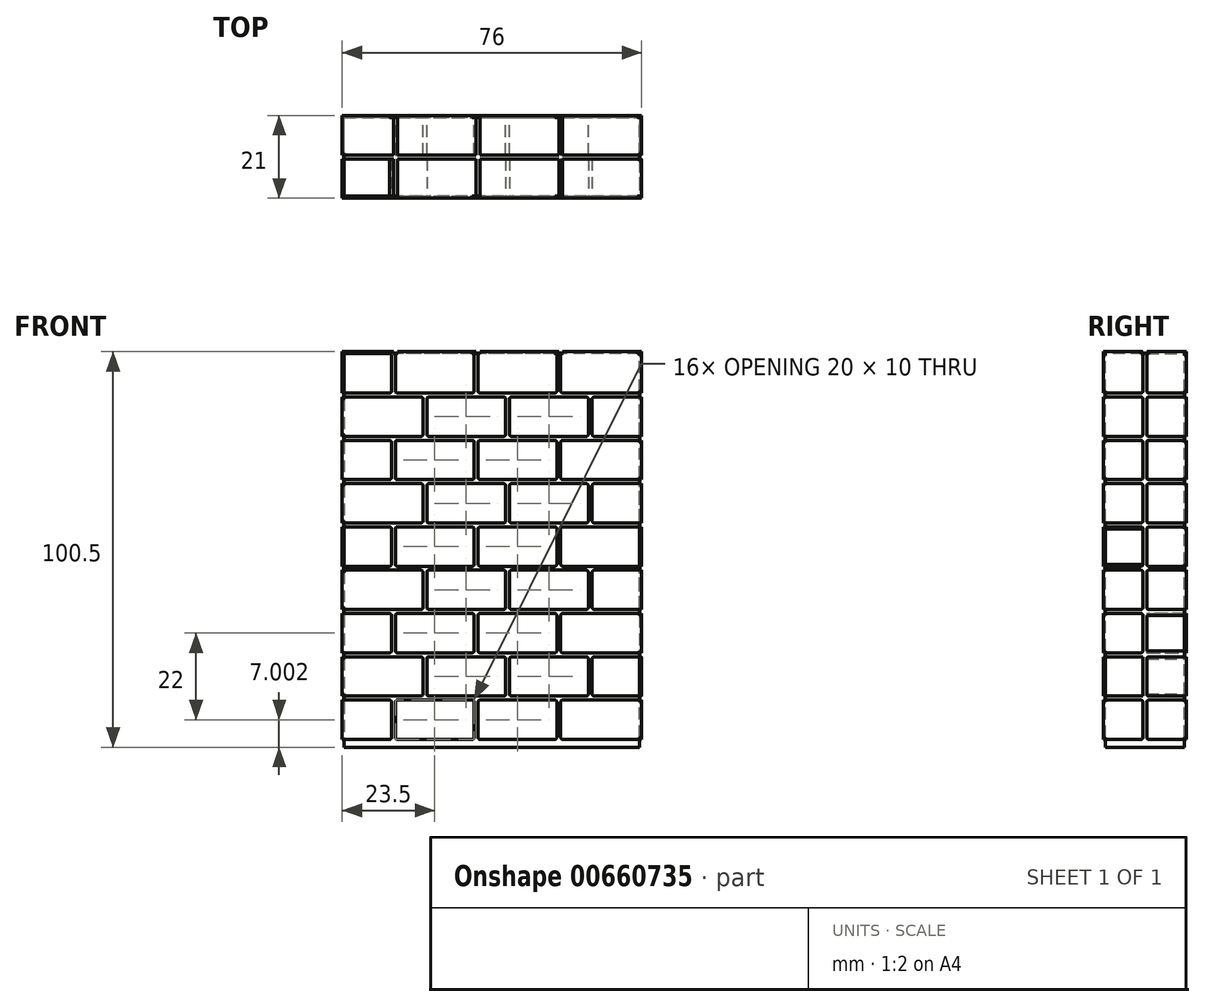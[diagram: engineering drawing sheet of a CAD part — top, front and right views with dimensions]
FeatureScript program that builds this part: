
annotation { "Feature Type Name" : "Feature", "Feature Type Description" : "" }
export const myFeature = defineFeature(function(context is Context, id is Id, definition is map)
    precondition{}
    {
        {
            var Q0;
            Q0=qCreatedBy(makeId("Front.planeOp"),FACE);
            var sketch = newSketch(context, id + "F0", { "sketchPlane" : qUnion([Q0])});
            skLineSegment(sketch, "E0.bottom", {"start": v(-37.59, 36.84) * mm, "end": v(37.41, 36.84) * mm});
            skLineSegment(sketch, "E0.top", {"start": v(-37.59, -63.16) * mm, "end": v(37.41, -63.16) * mm});
            skLineSegment(sketch, "E0.left", {"start": v(-37.59, 36.84) * mm, "end": v(-37.59, -63.16) * mm});
            skLineSegment(sketch, "E0.right", {"start": v(37.41, 36.84) * mm, "end": v(37.41, -63.16) * mm});
            skSolve(sketch);
        }
        {
            var Q0;
            Q0=makeQuery(id+"F0.imprint","IMPRINT",FACE,{"disambiguationData":[TD([[makeQuery(id+"F0.imprint","IMPRINT",EDGE,{"derivedFrom":sQuery(id+"F0.wireOp",EDGE,"E0.bottom")}),-1.0]])]});
            extrude(context, id + "F1", {"entities" : qUnion([Q0]), "endBound" : BoundingType.SYMMETRIC, "depth" : 20 * mm, "offsetDistance" : 25 * mm});
        }
        {
            var Q0;
            Q0=makeQuery(id+"F1.opExtrude","CAP_FACE",FACE,{"disambiguationData":[OSD([sQuery(id+"F0.wireOp",EDGE,"E0.bottom"),sQuery(id+"F0.wireOp",EDGE,"E0.top"),sQuery(id+"F0.wireOp",EDGE,"E0.left"),sQuery(id+"F0.wireOp",EDGE,"E0.right")])],"isStart":false});
            var sketch = newSketch(context, id + "F2", { "sketchPlane" : qUnion([Q0])});
            skLineSegment(sketch, "E1.bottom", {"start": v(36.91, 36.84) * mm, "end": v(17.91, 36.84) * mm});
            skLineSegment(sketch, "E1.top", {"start": v(36.91, 26.84) * mm, "end": v(17.91, 26.84) * mm});
            skLineSegment(sketch, "E1.left", {"start": v(37.41, 36.34) * mm, "end": v(37.41, 27.34) * mm});
            skLineSegment(sketch, "E1.right", {"start": v(17.41, 36.34) * mm, "end": v(17.41, 27.34) * mm});
            skPoint(sketch, "E2.visualSharp", {"position": v(17.41, 36.84) * mm});
            skArc(sketch, "E2.filletArc", {"start": v(17.91, 36.84) * mm, "mid": v(17.56, 36.7) * mm, "end": v(17.41, 36.34) * mm});
            skPoint(sketch, "E3.visualSharp", {"position": v(17.41, 26.84) * mm});
            skArc(sketch, "E3.filletArc", {"start": v(17.41, 27.34) * mm, "mid": v(17.56, 26.99) * mm, "end": v(17.91, 26.84) * mm});
            skPoint(sketch, "E4.visualSharp", {"position": v(37.41, 26.84) * mm});
            skArc(sketch, "E4.filletArc", {"start": v(36.91, 26.84) * mm, "mid": v(37.26, 26.99) * mm, "end": v(37.41, 27.34) * mm});
            skPoint(sketch, "E5.visualSharp", {"position": v(37.41, 36.84) * mm});
            skArc(sketch, "E5.filletArc", {"start": v(37.41, 36.34) * mm, "mid": v(37.26, 36.7) * mm, "end": v(36.91, 36.84) * mm});
            skLineSegment(sketch, "E6.1.0.0", {"start": v(-3.59, 36.34) * mm, "end": v(-3.59, 27.34) * mm});
            skLineSegment(sketch, "E6.1.0.1", {"start": v(15.91, 26.84) * mm, "end": v(-3.09, 26.84) * mm});
            skLineSegment(sketch, "E6.1.0.2", {"start": v(16.41, 36.34) * mm, "end": v(16.41, 27.34) * mm});
            skLineSegment(sketch, "E6.1.0.3", {"start": v(15.91, 36.84) * mm, "end": v(-3.09, 36.84) * mm});
            skArc(sketch, "E6.1.0.4", {"start": v(-3.59, 27.34) * mm, "mid": v(-3.44, 26.99) * mm, "end": v(-3.09, 26.84) * mm});
            skArc(sketch, "E6.1.0.5", {"start": v(-3.09, 36.84) * mm, "mid": v(-3.44, 36.7) * mm, "end": v(-3.59, 36.34) * mm});
            skArc(sketch, "E6.1.0.6", {"start": v(16.41, 36.34) * mm, "mid": v(16.26, 36.7) * mm, "end": v(15.91, 36.84) * mm});
            skArc(sketch, "E6.1.0.7", {"start": v(15.91, 26.84) * mm, "mid": v(16.26, 26.99) * mm, "end": v(16.41, 27.34) * mm});
            skLineSegment(sketch, "E6.2.0.0", {"start": v(-24.59, 36.34) * mm, "end": v(-24.59, 27.34) * mm});
            skLineSegment(sketch, "E6.2.0.1", {"start": v(-5.09, 26.84) * mm, "end": v(-24.09, 26.84) * mm});
            skLineSegment(sketch, "E6.2.0.2", {"start": v(-4.59, 36.34) * mm, "end": v(-4.59, 27.34) * mm});
            skLineSegment(sketch, "E6.2.0.3", {"start": v(-5.09, 36.84) * mm, "end": v(-24.09, 36.84) * mm});
            skArc(sketch, "E6.2.0.4", {"start": v(-24.59, 27.34) * mm, "mid": v(-24.44, 26.99) * mm, "end": v(-24.09, 26.84) * mm});
            skArc(sketch, "E6.2.0.5", {"start": v(-24.09, 36.84) * mm, "mid": v(-24.44, 36.7) * mm, "end": v(-24.59, 36.34) * mm});
            skArc(sketch, "E6.2.0.6", {"start": v(-4.59, 36.34) * mm, "mid": v(-4.74, 36.7) * mm, "end": v(-5.09, 36.84) * mm});
            skArc(sketch, "E6.2.0.7", {"start": v(-5.09, 26.84) * mm, "mid": v(-4.74, 26.99) * mm, "end": v(-4.59, 27.34) * mm});
            skLineSegment(sketch, "E6.3.0.0", {"start": v(-45.59, 36.34) * mm, "end": v(-45.59, 27.34) * mm});
            skLineSegment(sketch, "E6.3.0.1", {"start": v(-26.09, 26.84) * mm, "end": v(-45.09, 26.84) * mm});
            skLineSegment(sketch, "E6.3.0.2", {"start": v(-25.59, 36.34) * mm, "end": v(-25.59, 27.34) * mm});
            skLineSegment(sketch, "E6.3.0.3", {"start": v(-26.09, 36.84) * mm, "end": v(-45.09, 36.84) * mm});
            skArc(sketch, "E6.3.0.4", {"start": v(-45.59, 27.34) * mm, "mid": v(-45.44, 26.99) * mm, "end": v(-45.09, 26.84) * mm});
            skArc(sketch, "E6.3.0.5", {"start": v(-45.09, 36.84) * mm, "mid": v(-45.44, 36.7) * mm, "end": v(-45.59, 36.34) * mm});
            skArc(sketch, "E6.3.0.6", {"start": v(-25.59, 36.34) * mm, "mid": v(-25.74, 36.7) * mm, "end": v(-26.09, 36.84) * mm});
            skArc(sketch, "E6.3.0.7", {"start": v(-26.09, 26.84) * mm, "mid": v(-25.74, 26.99) * mm, "end": v(-25.59, 27.34) * mm});
            skLineSegment(sketch, "E6.direction1", {"start": v(17.41, 27.34) * mm, "end": v(-3.59, 27.34) * mm, "construction": true});
            skLineSegment(sketch, "E7.bottom", {"start": v(-37.09, 25.84) * mm, "end": v(-18.09, 25.84) * mm});
            skLineSegment(sketch, "E7.top", {"start": v(-37.09, 15.84) * mm, "end": v(-18.09, 15.84) * mm});
            skLineSegment(sketch, "E7.left", {"start": v(-37.59, 25.34) * mm, "end": v(-37.59, 16.34) * mm});
            skLineSegment(sketch, "E7.right", {"start": v(-17.59, 25.34) * mm, "end": v(-17.59, 16.34) * mm});
            skPoint(sketch, "E8.visualSharp", {"position": v(-37.59, 25.84) * mm});
            skArc(sketch, "E8.filletArc", {"start": v(-37.09, 25.84) * mm, "mid": v(-37.44, 25.7) * mm, "end": v(-37.59, 25.34) * mm});
            skPoint(sketch, "E9.visualSharp", {"position": v(-37.59, 15.84) * mm});
            skArc(sketch, "E9.filletArc", {"start": v(-37.59, 16.34) * mm, "mid": v(-37.44, 15.99) * mm, "end": v(-37.09, 15.84) * mm});
            skPoint(sketch, "E10.visualSharp", {"position": v(-17.59, 25.84) * mm});
            skArc(sketch, "E10.filletArc", {"start": v(-17.59, 25.34) * mm, "mid": v(-17.74, 25.7) * mm, "end": v(-18.09, 25.84) * mm});
            skPoint(sketch, "E11.visualSharp", {"position": v(-17.59, 15.84) * mm});
            skArc(sketch, "E11.filletArc", {"start": v(-18.09, 15.84) * mm, "mid": v(-17.74, 15.99) * mm, "end": v(-17.59, 16.34) * mm});
            skArc(sketch, "E12.1.0.0", {"start": v(-16.59, 16.34) * mm, "mid": v(-16.44, 15.99) * mm, "end": v(-16.09, 15.84) * mm});
            skLineSegment(sketch, "E12.1.0.1", {"start": v(-16.59, 25.34) * mm, "end": v(-16.59, 16.34) * mm});
            skArc(sketch, "E12.1.0.2", {"start": v(-16.09, 25.84) * mm, "mid": v(-16.44, 25.7) * mm, "end": v(-16.59, 25.34) * mm});
            skLineSegment(sketch, "E12.1.0.3", {"start": v(-16.09, 25.84) * mm, "end": v(2.91, 25.84) * mm});
            skArc(sketch, "E12.1.0.4", {"start": v(3.41, 25.34) * mm, "mid": v(3.26, 25.7) * mm, "end": v(2.91, 25.84) * mm});
            skLineSegment(sketch, "E12.1.0.5", {"start": v(3.41, 25.34) * mm, "end": v(3.41, 16.34) * mm});
            skArc(sketch, "E12.1.0.6", {"start": v(2.91, 15.84) * mm, "mid": v(3.26, 15.99) * mm, "end": v(3.41, 16.34) * mm});
            skLineSegment(sketch, "E12.1.0.7", {"start": v(-16.09, 15.84) * mm, "end": v(2.91, 15.84) * mm});
            skArc(sketch, "E12.2.0.0", {"start": v(4.41, 16.34) * mm, "mid": v(4.56, 15.99) * mm, "end": v(4.91, 15.84) * mm});
            skLineSegment(sketch, "E12.2.0.1", {"start": v(4.41, 25.34) * mm, "end": v(4.41, 16.34) * mm});
            skArc(sketch, "E12.2.0.2", {"start": v(4.91, 25.84) * mm, "mid": v(4.56, 25.7) * mm, "end": v(4.41, 25.34) * mm});
            skLineSegment(sketch, "E12.2.0.3", {"start": v(4.91, 25.84) * mm, "end": v(23.91, 25.84) * mm});
            skArc(sketch, "E12.2.0.4", {"start": v(24.41, 25.34) * mm, "mid": v(24.26, 25.7) * mm, "end": v(23.91, 25.84) * mm});
            skLineSegment(sketch, "E12.2.0.5", {"start": v(24.41, 25.34) * mm, "end": v(24.41, 16.34) * mm});
            skArc(sketch, "E12.2.0.6", {"start": v(23.91, 15.84) * mm, "mid": v(24.26, 15.99) * mm, "end": v(24.41, 16.34) * mm});
            skLineSegment(sketch, "E12.2.0.7", {"start": v(4.91, 15.84) * mm, "end": v(23.91, 15.84) * mm});
            skArc(sketch, "E12.3.0.0", {"start": v(25.41, 16.34) * mm, "mid": v(25.56, 15.99) * mm, "end": v(25.91, 15.84) * mm});
            skLineSegment(sketch, "E12.3.0.1", {"start": v(25.41, 25.34) * mm, "end": v(25.41, 16.34) * mm});
            skArc(sketch, "E12.3.0.2", {"start": v(25.91, 25.84) * mm, "mid": v(25.56, 25.7) * mm, "end": v(25.41, 25.34) * mm});
            skLineSegment(sketch, "E12.3.0.3", {"start": v(25.91, 25.84) * mm, "end": v(44.91, 25.84) * mm});
            skArc(sketch, "E12.3.0.4", {"start": v(45.41, 25.34) * mm, "mid": v(45.26, 25.7) * mm, "end": v(44.91, 25.84) * mm});
            skLineSegment(sketch, "E12.3.0.5", {"start": v(45.41, 25.34) * mm, "end": v(45.41, 16.34) * mm});
            skArc(sketch, "E12.3.0.6", {"start": v(44.91, 15.84) * mm, "mid": v(45.26, 15.99) * mm, "end": v(45.41, 16.34) * mm});
            skLineSegment(sketch, "E12.3.0.7", {"start": v(25.91, 15.84) * mm, "end": v(44.91, 15.84) * mm});
            skLineSegment(sketch, "E12.direction1", {"start": v(-37.09, 15.84) * mm, "end": v(-16.09, 15.84) * mm, "construction": true});
            skLineSegment(sketch, "E13.0.1.0", {"start": v(-25.59, 14.34) * mm, "end": v(-25.59, 5.34) * mm});
            skLineSegment(sketch, "E13.0.1.1", {"start": v(-16.59, 3.34) * mm, "end": v(-16.59, -5.66) * mm});
            skLineSegment(sketch, "E13.0.1.2", {"start": v(15.91, 4.84) * mm, "end": v(-3.09, 4.84) * mm});
            skLineSegment(sketch, "E13.0.1.3", {"start": v(24.41, 3.34) * mm, "end": v(24.41, -5.66) * mm});
            skLineSegment(sketch, "E13.0.1.4", {"start": v(15.91, 14.84) * mm, "end": v(-3.09, 14.84) * mm});
            skLineSegment(sketch, "E13.0.1.5", {"start": v(-3.59, 14.34) * mm, "end": v(-3.59, 5.34) * mm});
            skPoint(sketch, "E13.0.1.6", {"position": v(17.41, 4.84) * mm});
            skLineSegment(sketch, "E13.0.1.7", {"start": v(17.41, 14.34) * mm, "end": v(17.41, 5.34) * mm});
            skLineSegment(sketch, "E13.0.1.8", {"start": v(16.41, 14.34) * mm, "end": v(16.41, 5.34) * mm});
            skLineSegment(sketch, "E13.0.1.9", {"start": v(37.41, 14.34) * mm, "end": v(37.41, 5.34) * mm});
            skLineSegment(sketch, "E13.0.1.10", {"start": v(-45.59, 14.34) * mm, "end": v(-45.59, 5.34) * mm});
            skLineSegment(sketch, "E13.0.1.11", {"start": v(4.91, -6.16) * mm, "end": v(23.91, -6.16) * mm});
            skLineSegment(sketch, "E13.0.1.12", {"start": v(36.91, 4.84) * mm, "end": v(17.91, 4.84) * mm});
            skPoint(sketch, "E13.0.1.13", {"position": v(37.41, 4.84) * mm});
            skLineSegment(sketch, "E13.0.1.14", {"start": v(4.91, 3.84) * mm, "end": v(23.91, 3.84) * mm});
            skPoint(sketch, "E13.0.1.15", {"position": v(-37.59, 3.84) * mm});
            skLineSegment(sketch, "E13.0.1.16", {"start": v(25.41, 3.34) * mm, "end": v(25.41, -5.66) * mm});
            skLineSegment(sketch, "E13.0.1.17", {"start": v(-26.09, 4.84) * mm, "end": v(-45.09, 4.84) * mm});
            skPoint(sketch, "E13.0.1.18", {"position": v(-37.59, -6.16) * mm});
            skPoint(sketch, "E13.0.1.19", {"position": v(37.41, 14.84) * mm});
            skLineSegment(sketch, "E13.0.1.20", {"start": v(36.91, 14.84) * mm, "end": v(17.91, 14.84) * mm});
            skLineSegment(sketch, "E13.0.1.21", {"start": v(-17.59, 3.34) * mm, "end": v(-17.59, -5.66) * mm});
            skPoint(sketch, "E13.0.1.22", {"position": v(17.41, 14.84) * mm});
            skLineSegment(sketch, "E13.0.1.23", {"start": v(-5.09, 14.84) * mm, "end": v(-24.09, 14.84) * mm});
            skLineSegment(sketch, "E13.0.1.24", {"start": v(-37.59, 3.34) * mm, "end": v(-37.59, -5.66) * mm});
            skLineSegment(sketch, "E13.0.1.25", {"start": v(4.41, 3.34) * mm, "end": v(4.41, -5.66) * mm});
            skLineSegment(sketch, "E13.0.1.26", {"start": v(-4.59, 14.34) * mm, "end": v(-4.59, 5.34) * mm});
            skLineSegment(sketch, "E13.0.1.27", {"start": v(-37.09, -6.16) * mm, "end": v(-16.09, -6.16) * mm, "construction": true});
            skLineSegment(sketch, "E13.0.1.28", {"start": v(-5.09, 4.84) * mm, "end": v(-24.09, 4.84) * mm});
            skLineSegment(sketch, "E13.0.1.29", {"start": v(-37.09, 3.84) * mm, "end": v(-18.09, 3.84) * mm});
            skLineSegment(sketch, "E13.0.1.30", {"start": v(-24.59, 14.34) * mm, "end": v(-24.59, 5.34) * mm});
            skLineSegment(sketch, "E13.0.1.31", {"start": v(17.41, 5.34) * mm, "end": v(-3.59, 5.34) * mm, "construction": true});
            skLineSegment(sketch, "E13.0.1.32", {"start": v(-16.09, -6.16) * mm, "end": v(2.91, -6.16) * mm});
            skLineSegment(sketch, "E13.0.1.33", {"start": v(25.91, -6.16) * mm, "end": v(44.91, -6.16) * mm});
            skPoint(sketch, "E13.0.1.34", {"position": v(-17.59, 3.84) * mm});
            skLineSegment(sketch, "E13.0.1.35", {"start": v(3.41, 3.34) * mm, "end": v(3.41, -5.66) * mm});
            skLineSegment(sketch, "E13.0.1.36", {"start": v(45.41, 3.34) * mm, "end": v(45.41, -5.66) * mm});
            skLineSegment(sketch, "E13.0.1.37", {"start": v(-16.09, 3.84) * mm, "end": v(2.91, 3.84) * mm});
            skLineSegment(sketch, "E13.0.1.38", {"start": v(25.91, 3.84) * mm, "end": v(44.91, 3.84) * mm});
            skPoint(sketch, "E13.0.1.39", {"position": v(-17.59, -6.16) * mm});
            skLineSegment(sketch, "E13.0.1.40", {"start": v(-26.09, 14.84) * mm, "end": v(-45.09, 14.84) * mm});
            skLineSegment(sketch, "E13.0.1.41", {"start": v(-37.09, -6.16) * mm, "end": v(-18.09, -6.16) * mm});
            skArc(sketch, "E13.0.1.42", {"start": v(2.91, -6.16) * mm, "mid": v(3.26, -6.01) * mm, "end": v(3.41, -5.66) * mm});
            skArc(sketch, "E13.0.1.43", {"start": v(44.91, -6.16) * mm, "mid": v(45.26, -6.01) * mm, "end": v(45.41, -5.66) * mm});
            skArc(sketch, "E13.0.1.44", {"start": v(45.41, 3.34) * mm, "mid": v(45.26, 3.7) * mm, "end": v(44.91, 3.84) * mm});
            skArc(sketch, "E13.0.1.45", {"start": v(-16.59, -5.66) * mm, "mid": v(-16.44, -6.01) * mm, "end": v(-16.09, -6.16) * mm});
            skArc(sketch, "E13.0.1.46", {"start": v(-5.09, 4.84) * mm, "mid": v(-4.74, 4.99) * mm, "end": v(-4.59, 5.34) * mm});
            skArc(sketch, "E13.0.1.47", {"start": v(25.41, -5.66) * mm, "mid": v(25.56, -6.01) * mm, "end": v(25.91, -6.16) * mm});
            skArc(sketch, "E13.0.1.48", {"start": v(-4.59, 14.34) * mm, "mid": v(-4.74, 14.7) * mm, "end": v(-5.09, 14.84) * mm});
            skArc(sketch, "E13.0.1.49", {"start": v(37.41, 14.34) * mm, "mid": v(37.26, 14.7) * mm, "end": v(36.91, 14.84) * mm});
            skArc(sketch, "E13.0.1.50", {"start": v(23.91, -6.16) * mm, "mid": v(24.26, -6.01) * mm, "end": v(24.41, -5.66) * mm});
            skArc(sketch, "E13.0.1.51", {"start": v(36.91, 4.84) * mm, "mid": v(37.26, 4.99) * mm, "end": v(37.41, 5.34) * mm});
            skArc(sketch, "E13.0.1.52", {"start": v(17.91, 14.84) * mm, "mid": v(17.56, 14.7) * mm, "end": v(17.41, 14.34) * mm});
            skArc(sketch, "E13.0.1.53", {"start": v(24.41, 3.34) * mm, "mid": v(24.26, 3.7) * mm, "end": v(23.91, 3.84) * mm});
            skArc(sketch, "E13.0.1.54", {"start": v(-24.09, 14.84) * mm, "mid": v(-24.44, 14.7) * mm, "end": v(-24.59, 14.34) * mm});
            skArc(sketch, "E13.0.1.55", {"start": v(-37.09, 3.84) * mm, "mid": v(-37.44, 3.7) * mm, "end": v(-37.59, 3.34) * mm});
            skArc(sketch, "E13.0.1.56", {"start": v(-24.59, 5.34) * mm, "mid": v(-24.44, 4.99) * mm, "end": v(-24.09, 4.84) * mm});
            skArc(sketch, "E13.0.1.57", {"start": v(-3.59, 5.34) * mm, "mid": v(-3.44, 4.99) * mm, "end": v(-3.09, 4.84) * mm});
            skArc(sketch, "E13.0.1.58", {"start": v(-3.09, 14.84) * mm, "mid": v(-3.44, 14.7) * mm, "end": v(-3.59, 14.34) * mm});
            skArc(sketch, "E13.0.1.59", {"start": v(16.41, 14.34) * mm, "mid": v(16.26, 14.7) * mm, "end": v(15.91, 14.84) * mm});
            skArc(sketch, "E13.0.1.60", {"start": v(4.91, 3.84) * mm, "mid": v(4.56, 3.7) * mm, "end": v(4.41, 3.34) * mm});
            skArc(sketch, "E13.0.1.61", {"start": v(4.41, -5.66) * mm, "mid": v(4.56, -6.01) * mm, "end": v(4.91, -6.16) * mm});
            skArc(sketch, "E13.0.1.62", {"start": v(-26.09, 4.84) * mm, "mid": v(-25.74, 4.99) * mm, "end": v(-25.59, 5.34) * mm});
            skArc(sketch, "E13.0.1.63", {"start": v(-25.59, 14.34) * mm, "mid": v(-25.74, 14.7) * mm, "end": v(-26.09, 14.84) * mm});
            skArc(sketch, "E13.0.1.64", {"start": v(-45.59, 5.34) * mm, "mid": v(-45.44, 4.99) * mm, "end": v(-45.09, 4.84) * mm});
            skArc(sketch, "E13.0.1.65", {"start": v(3.41, 3.34) * mm, "mid": v(3.26, 3.7) * mm, "end": v(2.91, 3.84) * mm});
            skArc(sketch, "E13.0.1.66", {"start": v(-45.09, 14.84) * mm, "mid": v(-45.44, 14.7) * mm, "end": v(-45.59, 14.34) * mm});
            skArc(sketch, "E13.0.1.67", {"start": v(-16.09, 3.84) * mm, "mid": v(-16.44, 3.7) * mm, "end": v(-16.59, 3.34) * mm});
            skArc(sketch, "E13.0.1.68", {"start": v(25.91, 3.84) * mm, "mid": v(25.56, 3.7) * mm, "end": v(25.41, 3.34) * mm});
            skArc(sketch, "E13.0.1.69", {"start": v(-17.59, 3.34) * mm, "mid": v(-17.74, 3.7) * mm, "end": v(-18.09, 3.84) * mm});
            skArc(sketch, "E13.0.1.70", {"start": v(-37.59, -5.66) * mm, "mid": v(-37.44, -6.01) * mm, "end": v(-37.09, -6.16) * mm});
            skArc(sketch, "E13.0.1.71", {"start": v(17.41, 5.34) * mm, "mid": v(17.56, 4.99) * mm, "end": v(17.91, 4.84) * mm});
            skArc(sketch, "E13.0.1.72", {"start": v(-18.09, -6.16) * mm, "mid": v(-17.74, -6.01) * mm, "end": v(-17.59, -5.66) * mm});
            skArc(sketch, "E13.0.1.73", {"start": v(15.91, 4.84) * mm, "mid": v(16.26, 4.99) * mm, "end": v(16.41, 5.34) * mm});
            skLineSegment(sketch, "E13.0.2.0", {"start": v(-25.59, -7.66) * mm, "end": v(-25.59, -16.66) * mm});
            skLineSegment(sketch, "E13.0.2.1", {"start": v(-16.59, -18.66) * mm, "end": v(-16.59, -27.66) * mm});
            skLineSegment(sketch, "E13.0.2.2", {"start": v(15.91, -17.16) * mm, "end": v(-3.09, -17.16) * mm});
            skLineSegment(sketch, "E13.0.2.3", {"start": v(24.41, -18.66) * mm, "end": v(24.41, -27.66) * mm});
            skLineSegment(sketch, "E13.0.2.4", {"start": v(15.91, -7.16) * mm, "end": v(-3.09, -7.16) * mm});
            skLineSegment(sketch, "E13.0.2.5", {"start": v(-3.59, -7.66) * mm, "end": v(-3.59, -16.66) * mm});
            skPoint(sketch, "E13.0.2.6", {"position": v(17.41, -17.16) * mm});
            skLineSegment(sketch, "E13.0.2.7", {"start": v(17.41, -7.66) * mm, "end": v(17.41, -16.66) * mm});
            skLineSegment(sketch, "E13.0.2.8", {"start": v(16.41, -7.66) * mm, "end": v(16.41, -16.66) * mm});
            skLineSegment(sketch, "E13.0.2.9", {"start": v(37.41, -7.66) * mm, "end": v(37.41, -16.66) * mm});
            skLineSegment(sketch, "E13.0.2.10", {"start": v(-45.59, -7.66) * mm, "end": v(-45.59, -16.66) * mm});
            skLineSegment(sketch, "E13.0.2.11", {"start": v(4.91, -28.16) * mm, "end": v(23.91, -28.16) * mm});
            skLineSegment(sketch, "E13.0.2.12", {"start": v(36.91, -17.16) * mm, "end": v(17.91, -17.16) * mm});
            skPoint(sketch, "E13.0.2.13", {"position": v(37.41, -17.16) * mm});
            skLineSegment(sketch, "E13.0.2.14", {"start": v(4.91, -18.16) * mm, "end": v(23.91, -18.16) * mm});
            skPoint(sketch, "E13.0.2.15", {"position": v(-37.59, -18.16) * mm});
            skLineSegment(sketch, "E13.0.2.16", {"start": v(25.41, -18.66) * mm, "end": v(25.41, -27.66) * mm});
            skLineSegment(sketch, "E13.0.2.17", {"start": v(-26.09, -17.16) * mm, "end": v(-45.09, -17.16) * mm});
            skPoint(sketch, "E13.0.2.18", {"position": v(-37.59, -28.16) * mm});
            skPoint(sketch, "E13.0.2.19", {"position": v(37.41, -7.16) * mm});
            skLineSegment(sketch, "E13.0.2.20", {"start": v(36.91, -7.16) * mm, "end": v(17.91, -7.16) * mm});
            skLineSegment(sketch, "E13.0.2.21", {"start": v(-17.59, -18.66) * mm, "end": v(-17.59, -27.66) * mm});
            skPoint(sketch, "E13.0.2.22", {"position": v(17.41, -7.16) * mm});
            skLineSegment(sketch, "E13.0.2.23", {"start": v(-5.09, -7.16) * mm, "end": v(-24.09, -7.16) * mm});
            skLineSegment(sketch, "E13.0.2.24", {"start": v(-37.59, -18.66) * mm, "end": v(-37.59, -27.66) * mm});
            skLineSegment(sketch, "E13.0.2.25", {"start": v(4.41, -18.66) * mm, "end": v(4.41, -27.66) * mm});
            skLineSegment(sketch, "E13.0.2.26", {"start": v(-4.59, -7.66) * mm, "end": v(-4.59, -16.66) * mm});
            skLineSegment(sketch, "E13.0.2.27", {"start": v(-37.09, -28.16) * mm, "end": v(-16.09, -28.16) * mm, "construction": true});
            skLineSegment(sketch, "E13.0.2.28", {"start": v(-5.09, -17.16) * mm, "end": v(-24.09, -17.16) * mm});
            skLineSegment(sketch, "E13.0.2.29", {"start": v(-37.09, -18.16) * mm, "end": v(-18.09, -18.16) * mm});
            skLineSegment(sketch, "E13.0.2.30", {"start": v(-24.59, -7.66) * mm, "end": v(-24.59, -16.66) * mm});
            skLineSegment(sketch, "E13.0.2.31", {"start": v(17.41, -16.66) * mm, "end": v(-3.59, -16.66) * mm, "construction": true});
            skLineSegment(sketch, "E13.0.2.32", {"start": v(-16.09, -28.16) * mm, "end": v(2.91, -28.16) * mm});
            skLineSegment(sketch, "E13.0.2.33", {"start": v(25.91, -28.16) * mm, "end": v(44.91, -28.16) * mm});
            skPoint(sketch, "E13.0.2.34", {"position": v(-17.59, -18.16) * mm});
            skLineSegment(sketch, "E13.0.2.35", {"start": v(3.41, -18.66) * mm, "end": v(3.41, -27.66) * mm});
            skLineSegment(sketch, "E13.0.2.36", {"start": v(45.41, -18.66) * mm, "end": v(45.41, -27.66) * mm});
            skLineSegment(sketch, "E13.0.2.37", {"start": v(-16.09, -18.16) * mm, "end": v(2.91, -18.16) * mm});
            skLineSegment(sketch, "E13.0.2.38", {"start": v(25.91, -18.16) * mm, "end": v(44.91, -18.16) * mm});
            skPoint(sketch, "E13.0.2.39", {"position": v(-17.59, -28.16) * mm});
            skLineSegment(sketch, "E13.0.2.40", {"start": v(-26.09, -7.16) * mm, "end": v(-45.09, -7.16) * mm});
            skLineSegment(sketch, "E13.0.2.41", {"start": v(-37.09, -28.16) * mm, "end": v(-18.09, -28.16) * mm});
            skArc(sketch, "E13.0.2.42", {"start": v(2.91, -28.16) * mm, "mid": v(3.26, -28.01) * mm, "end": v(3.41, -27.66) * mm});
            skArc(sketch, "E13.0.2.43", {"start": v(44.91, -28.16) * mm, "mid": v(45.26, -28.01) * mm, "end": v(45.41, -27.66) * mm});
            skArc(sketch, "E13.0.2.44", {"start": v(45.41, -18.66) * mm, "mid": v(45.26, -18.3) * mm, "end": v(44.91, -18.16) * mm});
            skArc(sketch, "E13.0.2.45", {"start": v(-16.59, -27.66) * mm, "mid": v(-16.44, -28.01) * mm, "end": v(-16.09, -28.16) * mm});
            skArc(sketch, "E13.0.2.46", {"start": v(-5.09, -17.16) * mm, "mid": v(-4.74, -17.01) * mm, "end": v(-4.59, -16.66) * mm});
            skArc(sketch, "E13.0.2.47", {"start": v(25.41, -27.66) * mm, "mid": v(25.56, -28.01) * mm, "end": v(25.91, -28.16) * mm});
            skArc(sketch, "E13.0.2.48", {"start": v(-4.59, -7.66) * mm, "mid": v(-4.74, -7.3) * mm, "end": v(-5.09, -7.16) * mm});
            skArc(sketch, "E13.0.2.49", {"start": v(37.41, -7.66) * mm, "mid": v(37.26, -7.3) * mm, "end": v(36.91, -7.16) * mm});
            skArc(sketch, "E13.0.2.50", {"start": v(23.91, -28.16) * mm, "mid": v(24.26, -28.01) * mm, "end": v(24.41, -27.66) * mm});
            skArc(sketch, "E13.0.2.51", {"start": v(36.91, -17.16) * mm, "mid": v(37.26, -17.01) * mm, "end": v(37.41, -16.66) * mm});
            skArc(sketch, "E13.0.2.52", {"start": v(17.91, -7.16) * mm, "mid": v(17.56, -7.3) * mm, "end": v(17.41, -7.66) * mm});
            skArc(sketch, "E13.0.2.53", {"start": v(24.41, -18.66) * mm, "mid": v(24.26, -18.3) * mm, "end": v(23.91, -18.16) * mm});
            skArc(sketch, "E13.0.2.54", {"start": v(-24.09, -7.16) * mm, "mid": v(-24.44, -7.3) * mm, "end": v(-24.59, -7.66) * mm});
            skArc(sketch, "E13.0.2.55", {"start": v(-37.09, -18.16) * mm, "mid": v(-37.44, -18.3) * mm, "end": v(-37.59, -18.66) * mm});
            skArc(sketch, "E13.0.2.56", {"start": v(-24.59, -16.66) * mm, "mid": v(-24.44, -17.01) * mm, "end": v(-24.09, -17.16) * mm});
            skArc(sketch, "E13.0.2.57", {"start": v(-3.59, -16.66) * mm, "mid": v(-3.44, -17.01) * mm, "end": v(-3.09, -17.16) * mm});
            skArc(sketch, "E13.0.2.58", {"start": v(-3.09, -7.16) * mm, "mid": v(-3.44, -7.3) * mm, "end": v(-3.59, -7.66) * mm});
            skArc(sketch, "E13.0.2.59", {"start": v(16.41, -7.66) * mm, "mid": v(16.26, -7.3) * mm, "end": v(15.91, -7.16) * mm});
            skArc(sketch, "E13.0.2.60", {"start": v(4.91, -18.16) * mm, "mid": v(4.56, -18.3) * mm, "end": v(4.41, -18.66) * mm});
            skArc(sketch, "E13.0.2.61", {"start": v(4.41, -27.66) * mm, "mid": v(4.56, -28.01) * mm, "end": v(4.91, -28.16) * mm});
            skArc(sketch, "E13.0.2.62", {"start": v(-26.09, -17.16) * mm, "mid": v(-25.74, -17.01) * mm, "end": v(-25.59, -16.66) * mm});
            skArc(sketch, "E13.0.2.63", {"start": v(-25.59, -7.66) * mm, "mid": v(-25.74, -7.3) * mm, "end": v(-26.09, -7.16) * mm});
            skArc(sketch, "E13.0.2.64", {"start": v(-45.59, -16.66) * mm, "mid": v(-45.44, -17.01) * mm, "end": v(-45.09, -17.16) * mm});
            skArc(sketch, "E13.0.2.65", {"start": v(3.41, -18.66) * mm, "mid": v(3.26, -18.3) * mm, "end": v(2.91, -18.16) * mm});
            skArc(sketch, "E13.0.2.66", {"start": v(-45.09, -7.16) * mm, "mid": v(-45.44, -7.3) * mm, "end": v(-45.59, -7.66) * mm});
            skArc(sketch, "E13.0.2.67", {"start": v(-16.09, -18.16) * mm, "mid": v(-16.44, -18.3) * mm, "end": v(-16.59, -18.66) * mm});
            skArc(sketch, "E13.0.2.68", {"start": v(25.91, -18.16) * mm, "mid": v(25.56, -18.3) * mm, "end": v(25.41, -18.66) * mm});
            skArc(sketch, "E13.0.2.69", {"start": v(-17.59, -18.66) * mm, "mid": v(-17.74, -18.3) * mm, "end": v(-18.09, -18.16) * mm});
            skArc(sketch, "E13.0.2.70", {"start": v(-37.59, -27.66) * mm, "mid": v(-37.44, -28.01) * mm, "end": v(-37.09, -28.16) * mm});
            skArc(sketch, "E13.0.2.71", {"start": v(17.41, -16.66) * mm, "mid": v(17.56, -17.01) * mm, "end": v(17.91, -17.16) * mm});
            skArc(sketch, "E13.0.2.72", {"start": v(-18.09, -28.16) * mm, "mid": v(-17.74, -28.01) * mm, "end": v(-17.59, -27.66) * mm});
            skArc(sketch, "E13.0.2.73", {"start": v(15.91, -17.16) * mm, "mid": v(16.26, -17.01) * mm, "end": v(16.41, -16.66) * mm});
            skLineSegment(sketch, "E13.0.3.0", {"start": v(-25.59, -29.66) * mm, "end": v(-25.59, -38.66) * mm});
            skLineSegment(sketch, "E13.0.3.1", {"start": v(-16.59, -40.66) * mm, "end": v(-16.59, -49.66) * mm});
            skLineSegment(sketch, "E13.0.3.2", {"start": v(15.91, -39.16) * mm, "end": v(-3.09, -39.16) * mm});
            skLineSegment(sketch, "E13.0.3.3", {"start": v(24.41, -40.66) * mm, "end": v(24.41, -49.66) * mm});
            skLineSegment(sketch, "E13.0.3.4", {"start": v(15.91, -29.16) * mm, "end": v(-3.09, -29.16) * mm});
            skLineSegment(sketch, "E13.0.3.5", {"start": v(-3.59, -29.66) * mm, "end": v(-3.59, -38.66) * mm});
            skPoint(sketch, "E13.0.3.6", {"position": v(17.41, -39.16) * mm});
            skLineSegment(sketch, "E13.0.3.7", {"start": v(17.41, -29.66) * mm, "end": v(17.41, -38.66) * mm});
            skLineSegment(sketch, "E13.0.3.8", {"start": v(16.41, -29.66) * mm, "end": v(16.41, -38.66) * mm});
            skLineSegment(sketch, "E13.0.3.9", {"start": v(37.41, -29.66) * mm, "end": v(37.41, -38.66) * mm});
            skLineSegment(sketch, "E13.0.3.10", {"start": v(-45.59, -29.66) * mm, "end": v(-45.59, -38.66) * mm});
            skLineSegment(sketch, "E13.0.3.11", {"start": v(4.91, -50.16) * mm, "end": v(23.91, -50.16) * mm});
            skLineSegment(sketch, "E13.0.3.12", {"start": v(36.91, -39.16) * mm, "end": v(17.91, -39.16) * mm});
            skPoint(sketch, "E13.0.3.13", {"position": v(37.41, -39.16) * mm});
            skLineSegment(sketch, "E13.0.3.14", {"start": v(4.91, -40.16) * mm, "end": v(23.91, -40.16) * mm});
            skPoint(sketch, "E13.0.3.15", {"position": v(-37.59, -40.16) * mm});
            skLineSegment(sketch, "E13.0.3.16", {"start": v(25.41, -40.66) * mm, "end": v(25.41, -49.66) * mm});
            skLineSegment(sketch, "E13.0.3.17", {"start": v(-26.09, -39.16) * mm, "end": v(-45.09, -39.16) * mm});
            skPoint(sketch, "E13.0.3.18", {"position": v(-37.59, -50.16) * mm});
            skPoint(sketch, "E13.0.3.19", {"position": v(37.41, -29.16) * mm});
            skLineSegment(sketch, "E13.0.3.20", {"start": v(36.91, -29.16) * mm, "end": v(17.91, -29.16) * mm});
            skLineSegment(sketch, "E13.0.3.21", {"start": v(-17.59, -40.66) * mm, "end": v(-17.59, -49.66) * mm});
            skPoint(sketch, "E13.0.3.22", {"position": v(17.41, -29.16) * mm});
            skLineSegment(sketch, "E13.0.3.23", {"start": v(-5.09, -29.16) * mm, "end": v(-24.09, -29.16) * mm});
            skLineSegment(sketch, "E13.0.3.24", {"start": v(-37.59, -40.66) * mm, "end": v(-37.59, -49.66) * mm});
            skLineSegment(sketch, "E13.0.3.25", {"start": v(4.41, -40.66) * mm, "end": v(4.41, -49.66) * mm});
            skLineSegment(sketch, "E13.0.3.26", {"start": v(-4.59, -29.66) * mm, "end": v(-4.59, -38.66) * mm});
            skLineSegment(sketch, "E13.0.3.27", {"start": v(-37.09, -50.16) * mm, "end": v(-16.09, -50.16) * mm, "construction": true});
            skLineSegment(sketch, "E13.0.3.28", {"start": v(-5.09, -39.16) * mm, "end": v(-24.09, -39.16) * mm});
            skLineSegment(sketch, "E13.0.3.29", {"start": v(-37.09, -40.16) * mm, "end": v(-18.09, -40.16) * mm});
            skLineSegment(sketch, "E13.0.3.30", {"start": v(-24.59, -29.66) * mm, "end": v(-24.59, -38.66) * mm});
            skLineSegment(sketch, "E13.0.3.31", {"start": v(17.41, -38.66) * mm, "end": v(-3.59, -38.66) * mm, "construction": true});
            skLineSegment(sketch, "E13.0.3.32", {"start": v(-16.09, -50.16) * mm, "end": v(2.91, -50.16) * mm});
            skLineSegment(sketch, "E13.0.3.33", {"start": v(25.91, -50.16) * mm, "end": v(44.91, -50.16) * mm});
            skPoint(sketch, "E13.0.3.34", {"position": v(-17.59, -40.16) * mm});
            skLineSegment(sketch, "E13.0.3.35", {"start": v(3.41, -40.66) * mm, "end": v(3.41, -49.66) * mm});
            skLineSegment(sketch, "E13.0.3.36", {"start": v(45.41, -40.66) * mm, "end": v(45.41, -49.66) * mm});
            skLineSegment(sketch, "E13.0.3.37", {"start": v(-16.09, -40.16) * mm, "end": v(2.91, -40.16) * mm});
            skLineSegment(sketch, "E13.0.3.38", {"start": v(25.91, -40.16) * mm, "end": v(44.91, -40.16) * mm});
            skPoint(sketch, "E13.0.3.39", {"position": v(-17.59, -50.16) * mm});
            skLineSegment(sketch, "E13.0.3.40", {"start": v(-26.09, -29.16) * mm, "end": v(-45.09, -29.16) * mm});
            skLineSegment(sketch, "E13.0.3.41", {"start": v(-37.09, -50.16) * mm, "end": v(-18.09, -50.16) * mm});
            skArc(sketch, "E13.0.3.42", {"start": v(2.91, -50.16) * mm, "mid": v(3.26, -50.01) * mm, "end": v(3.41, -49.66) * mm});
            skArc(sketch, "E13.0.3.43", {"start": v(44.91, -50.16) * mm, "mid": v(45.26, -50.01) * mm, "end": v(45.41, -49.66) * mm});
            skArc(sketch, "E13.0.3.44", {"start": v(45.41, -40.66) * mm, "mid": v(45.26, -40.3) * mm, "end": v(44.91, -40.16) * mm});
            skArc(sketch, "E13.0.3.45", {"start": v(-16.59, -49.66) * mm, "mid": v(-16.44, -50.01) * mm, "end": v(-16.09, -50.16) * mm});
            skArc(sketch, "E13.0.3.46", {"start": v(-5.09, -39.16) * mm, "mid": v(-4.74, -39.01) * mm, "end": v(-4.59, -38.66) * mm});
            skArc(sketch, "E13.0.3.47", {"start": v(25.41, -49.66) * mm, "mid": v(25.56, -50.01) * mm, "end": v(25.91, -50.16) * mm});
            skArc(sketch, "E13.0.3.48", {"start": v(-4.59, -29.66) * mm, "mid": v(-4.74, -29.3) * mm, "end": v(-5.09, -29.16) * mm});
            skArc(sketch, "E13.0.3.49", {"start": v(37.41, -29.66) * mm, "mid": v(37.26, -29.3) * mm, "end": v(36.91, -29.16) * mm});
            skArc(sketch, "E13.0.3.50", {"start": v(23.91, -50.16) * mm, "mid": v(24.26, -50.01) * mm, "end": v(24.41, -49.66) * mm});
            skArc(sketch, "E13.0.3.51", {"start": v(36.91, -39.16) * mm, "mid": v(37.26, -39.01) * mm, "end": v(37.41, -38.66) * mm});
            skArc(sketch, "E13.0.3.52", {"start": v(17.91, -29.16) * mm, "mid": v(17.56, -29.3) * mm, "end": v(17.41, -29.66) * mm});
            skArc(sketch, "E13.0.3.53", {"start": v(24.41, -40.66) * mm, "mid": v(24.26, -40.3) * mm, "end": v(23.91, -40.16) * mm});
            skArc(sketch, "E13.0.3.54", {"start": v(-24.09, -29.16) * mm, "mid": v(-24.44, -29.3) * mm, "end": v(-24.59, -29.66) * mm});
            skArc(sketch, "E13.0.3.55", {"start": v(-37.09, -40.16) * mm, "mid": v(-37.44, -40.3) * mm, "end": v(-37.59, -40.66) * mm});
            skArc(sketch, "E13.0.3.56", {"start": v(-24.59, -38.66) * mm, "mid": v(-24.44, -39.01) * mm, "end": v(-24.09, -39.16) * mm});
            skArc(sketch, "E13.0.3.57", {"start": v(-3.59, -38.66) * mm, "mid": v(-3.44, -39.01) * mm, "end": v(-3.09, -39.16) * mm});
            skArc(sketch, "E13.0.3.58", {"start": v(-3.09, -29.16) * mm, "mid": v(-3.44, -29.3) * mm, "end": v(-3.59, -29.66) * mm});
            skArc(sketch, "E13.0.3.59", {"start": v(16.41, -29.66) * mm, "mid": v(16.26, -29.3) * mm, "end": v(15.91, -29.16) * mm});
            skArc(sketch, "E13.0.3.60", {"start": v(4.91, -40.16) * mm, "mid": v(4.56, -40.3) * mm, "end": v(4.41, -40.66) * mm});
            skArc(sketch, "E13.0.3.61", {"start": v(4.41, -49.66) * mm, "mid": v(4.56, -50.01) * mm, "end": v(4.91, -50.16) * mm});
            skArc(sketch, "E13.0.3.62", {"start": v(-26.09, -39.16) * mm, "mid": v(-25.74, -39.01) * mm, "end": v(-25.59, -38.66) * mm});
            skArc(sketch, "E13.0.3.63", {"start": v(-25.59, -29.66) * mm, "mid": v(-25.74, -29.3) * mm, "end": v(-26.09, -29.16) * mm});
            skArc(sketch, "E13.0.3.64", {"start": v(-45.59, -38.66) * mm, "mid": v(-45.44, -39.01) * mm, "end": v(-45.09, -39.16) * mm});
            skArc(sketch, "E13.0.3.65", {"start": v(3.41, -40.66) * mm, "mid": v(3.26, -40.3) * mm, "end": v(2.91, -40.16) * mm});
            skArc(sketch, "E13.0.3.66", {"start": v(-45.09, -29.16) * mm, "mid": v(-45.44, -29.3) * mm, "end": v(-45.59, -29.66) * mm});
            skArc(sketch, "E13.0.3.67", {"start": v(-16.09, -40.16) * mm, "mid": v(-16.44, -40.3) * mm, "end": v(-16.59, -40.66) * mm});
            skArc(sketch, "E13.0.3.68", {"start": v(25.91, -40.16) * mm, "mid": v(25.56, -40.3) * mm, "end": v(25.41, -40.66) * mm});
            skArc(sketch, "E13.0.3.69", {"start": v(-17.59, -40.66) * mm, "mid": v(-17.74, -40.3) * mm, "end": v(-18.09, -40.16) * mm});
            skArc(sketch, "E13.0.3.70", {"start": v(-37.59, -49.66) * mm, "mid": v(-37.44, -50.01) * mm, "end": v(-37.09, -50.16) * mm});
            skArc(sketch, "E13.0.3.71", {"start": v(17.41, -38.66) * mm, "mid": v(17.56, -39.01) * mm, "end": v(17.91, -39.16) * mm});
            skArc(sketch, "E13.0.3.72", {"start": v(-18.09, -50.16) * mm, "mid": v(-17.74, -50.01) * mm, "end": v(-17.59, -49.66) * mm});
            skArc(sketch, "E13.0.3.73", {"start": v(15.91, -39.16) * mm, "mid": v(16.26, -39.01) * mm, "end": v(16.41, -38.66) * mm});
            skLineSegment(sketch, "E13.direction1", {"start": v(-37.59, 15.84) * mm, "end": v(-12.59, 15.84) * mm, "construction": true});
            skLineSegment(sketch, "E13.direction2", {"start": v(-37.59, 15.84) * mm, "end": v(-37.59, -6.16) * mm, "construction": true});
            skLineSegment(sketch, "E14.0.1.0", {"start": v(36.91, -61.16) * mm, "end": v(17.91, -61.16) * mm});
            skPoint(sketch, "E14.0.1.1", {"position": v(17.41, -51.16) * mm});
            skLineSegment(sketch, "E14.0.1.2", {"start": v(-26.09, -61.16) * mm, "end": v(-45.09, -61.16) * mm});
            skLineSegment(sketch, "E14.0.1.3", {"start": v(-45.59, -51.66) * mm, "end": v(-45.59, -60.66) * mm});
            skLineSegment(sketch, "E14.0.1.4", {"start": v(36.91, -51.16) * mm, "end": v(17.91, -51.16) * mm});
            skLineSegment(sketch, "E14.0.1.5", {"start": v(17.41, -60.66) * mm, "end": v(-3.59, -60.66) * mm, "construction": true});
            skPoint(sketch, "E14.0.1.6", {"position": v(-17.59, -62.16) * mm});
            skPoint(sketch, "E14.0.1.7", {"position": v(37.41, -61.16) * mm});
            skPoint(sketch, "E14.0.1.8", {"position": v(37.41, -51.16) * mm});
            skLineSegment(sketch, "E14.0.1.9", {"start": v(16.41, -51.66) * mm, "end": v(16.41, -60.66) * mm});
            skLineSegment(sketch, "E14.0.1.10", {"start": v(-26.09, -51.16) * mm, "end": v(-45.09, -51.16) * mm});
            skLineSegment(sketch, "E14.0.1.11", {"start": v(-25.59, -51.66) * mm, "end": v(-25.59, -60.66) * mm});
            skLineSegment(sketch, "E14.0.1.13", {"start": v(-5.09, -51.16) * mm, "end": v(-24.09, -51.16) * mm});
            skLineSegment(sketch, "E14.0.1.14", {"start": v(15.91, -61.16) * mm, "end": v(-3.09, -61.16) * mm});
            skLineSegment(sketch, "E14.0.1.15", {"start": v(15.91, -51.16) * mm, "end": v(-3.09, -51.16) * mm});
            skLineSegment(sketch, "E14.0.1.16", {"start": v(-24.59, -51.66) * mm, "end": v(-24.59, -60.66) * mm});
            skLineSegment(sketch, "E14.0.1.17", {"start": v(37.41, -51.66) * mm, "end": v(37.41, -60.66) * mm});
            skLineSegment(sketch, "E14.0.1.18", {"start": v(-4.59, -51.66) * mm, "end": v(-4.59, -60.66) * mm});
            skLineSegment(sketch, "E14.0.1.19", {"start": v(-3.59, -51.66) * mm, "end": v(-3.59, -60.66) * mm});
            skPoint(sketch, "E14.0.1.20", {"position": v(-37.59, -62.16) * mm});
            skLineSegment(sketch, "E14.0.1.22", {"start": v(17.41, -51.66) * mm, "end": v(17.41, -60.66) * mm});
            skPoint(sketch, "E14.0.1.23", {"position": v(17.41, -61.16) * mm});
            skLineSegment(sketch, "E14.0.1.24", {"start": v(-5.09, -61.16) * mm, "end": v(-24.09, -61.16) * mm});
            skArc(sketch, "E14.0.1.25", {"start": v(-24.09, -51.16) * mm, "mid": v(-24.44, -51.3) * mm, "end": v(-24.59, -51.66) * mm});
            skArc(sketch, "E14.0.1.26", {"start": v(-25.59, -51.66) * mm, "mid": v(-25.74, -51.3) * mm, "end": v(-26.09, -51.16) * mm});
            skArc(sketch, "E14.0.1.27", {"start": v(-24.59, -60.66) * mm, "mid": v(-24.44, -61.01) * mm, "end": v(-24.09, -61.16) * mm});
            skArc(sketch, "E14.0.1.28", {"start": v(-3.09, -51.16) * mm, "mid": v(-3.44, -51.3) * mm, "end": v(-3.59, -51.66) * mm});
            skArc(sketch, "E14.0.1.29", {"start": v(36.91, -61.16) * mm, "mid": v(37.26, -61.01) * mm, "end": v(37.41, -60.66) * mm});
            skArc(sketch, "E14.0.1.30", {"start": v(17.41, -60.66) * mm, "mid": v(17.56, -61.01) * mm, "end": v(17.91, -61.16) * mm});
            skArc(sketch, "E14.0.1.31", {"start": v(17.91, -51.16) * mm, "mid": v(17.56, -51.3) * mm, "end": v(17.41, -51.66) * mm});
            skArc(sketch, "E14.0.1.32", {"start": v(-45.09, -51.16) * mm, "mid": v(-45.44, -51.3) * mm, "end": v(-45.59, -51.66) * mm});
            skArc(sketch, "E14.0.1.33", {"start": v(15.91, -61.16) * mm, "mid": v(16.26, -61.01) * mm, "end": v(16.41, -60.66) * mm});
            skArc(sketch, "E14.0.1.34", {"start": v(-3.59, -60.66) * mm, "mid": v(-3.44, -61.01) * mm, "end": v(-3.09, -61.16) * mm});
            skArc(sketch, "E14.0.1.35", {"start": v(16.41, -51.66) * mm, "mid": v(16.26, -51.3) * mm, "end": v(15.91, -51.16) * mm});
            skArc(sketch, "E14.0.1.36", {"start": v(-45.59, -60.66) * mm, "mid": v(-45.44, -61.01) * mm, "end": v(-45.09, -61.16) * mm});
            skArc(sketch, "E14.0.1.37", {"start": v(-4.59, -51.66) * mm, "mid": v(-4.74, -51.3) * mm, "end": v(-5.09, -51.16) * mm});
            skArc(sketch, "E14.0.1.38", {"start": v(-26.09, -61.16) * mm, "mid": v(-25.74, -61.01) * mm, "end": v(-25.59, -60.66) * mm});
            skArc(sketch, "E14.0.1.39", {"start": v(-5.09, -61.16) * mm, "mid": v(-4.74, -61.01) * mm, "end": v(-4.59, -60.66) * mm});
            skArc(sketch, "E14.0.1.40", {"start": v(37.41, -51.66) * mm, "mid": v(37.26, -51.3) * mm, "end": v(36.91, -51.16) * mm});
            skLineSegment(sketch, "E14.direction1", {"start": v(-45.09, -39.16) * mm, "end": v(-20.09, -39.16) * mm, "construction": true});
            skLineSegment(sketch, "E14.direction2", {"start": v(-45.09, -39.16) * mm, "end": v(-45.09, -61.16) * mm, "construction": true});
            skSolve(sketch);
        }
        {
            var Q0;
            Q0=makeQuery(id+"F2.imprint","IMPRINT",FACE,{"disambiguationData":[TD([[makeQuery(id+"F2.imprint","IMPRINT",EDGE,{"derivedFrom":sQuery(id+"F2.wireOp",EDGE,"E6.3.0.2")}),-1.0]])]});
            var Q1;
            Q1=makeQuery(id+"F2.imprint","IMPRINT",FACE,{"disambiguationData":[TD([[makeQuery(id+"F2.imprint","IMPRINT",EDGE,{"derivedFrom":sQuery(id+"F2.wireOp",EDGE,"E6.2.0.0")}),1.0]])]});
            var Q2;
            Q2=makeQuery(id+"F2.imprint","IMPRINT",FACE,{"disambiguationData":[TD([[makeQuery(id+"F2.imprint","IMPRINT",EDGE,{"derivedFrom":sQuery(id+"F2.wireOp",EDGE,"E6.1.0.0")}),1.0]])]});
            var Q3;
            Q3=makeQuery(id+"F2.imprint","IMPRINT",FACE,{"disambiguationData":[TD([[makeQuery(id+"F2.imprint","IMPRINT",EDGE,{"derivedFrom":sQuery(id+"F2.wireOp",EDGE,"E1.bottom")}),-1.0]])]});
            var Q4;
            {var subQ6=sQuery(id+"F2.wireOp",EDGE,"E12.3.0.0");Q4=makeQuery(id+"F2.imprint","IMPRINT",FACE,{"disambiguationData":[TD([[makeQuery(id+"F2.imprint","IMPRINT",EDGE,{"derivedFrom":subQ6}),1.0]])]});}
            var Q5;
            Q5=makeQuery(id+"F2.imprint","IMPRINT",FACE,{"disambiguationData":[TD([[makeQuery(id+"F2.imprint","IMPRINT",EDGE,{"derivedFrom":sQuery(id+"F2.wireOp",EDGE,"E12.2.0.0")}),1.0]])]});
            var Q6;
            Q6=makeQuery(id+"F2.imprint","IMPRINT",FACE,{"disambiguationData":[TD([[makeQuery(id+"F2.imprint","IMPRINT",EDGE,{"derivedFrom":sQuery(id+"F2.wireOp",EDGE,"E12.1.0.0")}),1.0]])]});
            var Q7;
            Q7=makeQuery(id+"F2.imprint","IMPRINT",FACE,{"disambiguationData":[TD([[makeQuery(id+"F2.imprint","IMPRINT",EDGE,{"derivedFrom":sQuery(id+"F2.wireOp",EDGE,"E7.bottom")}),-1.0]])]});
            var Q8;
            Q8=makeQuery(id+"F2.imprint","IMPRINT",FACE,{"disambiguationData":[TD([[makeQuery(id+"F2.imprint","IMPRINT",EDGE,{"derivedFrom":sQuery(id+"F2.wireOp",EDGE,"E13.0.1.0")}),-1.0]])]});
            var Q9;
            Q9=makeQuery(id+"F2.imprint","IMPRINT",FACE,{"disambiguationData":[TD([[makeQuery(id+"F2.imprint","IMPRINT",EDGE,{"derivedFrom":sQuery(id+"F2.wireOp",EDGE,"E13.0.1.23")}),1.0]])]});
            var Q10;
            Q10=makeQuery(id+"F2.imprint","IMPRINT",FACE,{"disambiguationData":[TD([[makeQuery(id+"F2.imprint","IMPRINT",EDGE,{"derivedFrom":sQuery(id+"F2.wireOp",EDGE,"E13.0.1.2")}),-1.0]])]});
            var Q11;
            Q11=makeQuery(id+"F2.imprint","IMPRINT",FACE,{"disambiguationData":[TD([[makeQuery(id+"F2.imprint","IMPRINT",EDGE,{"derivedFrom":sQuery(id+"F2.wireOp",EDGE,"E13.0.1.7")}),1.0]])]});
            var Q12;
            Q12=makeQuery(id+"F2.imprint","IMPRINT",FACE,{"disambiguationData":[TD([[makeQuery(id+"F2.imprint","IMPRINT",EDGE,{"derivedFrom":sQuery(id+"F2.wireOp",EDGE,"E13.0.1.16")}),1.0]])]});
            var Q13;
            Q13=makeQuery(id+"F2.imprint","IMPRINT",FACE,{"disambiguationData":[TD([[makeQuery(id+"F2.imprint","IMPRINT",EDGE,{"derivedFrom":sQuery(id+"F2.wireOp",EDGE,"E13.0.1.3")}),-1.0]])]});
            var Q14;
            Q14=makeQuery(id+"F2.imprint","IMPRINT",FACE,{"disambiguationData":[TD([[makeQuery(id+"F2.imprint","IMPRINT",EDGE,{"derivedFrom":sQuery(id+"F2.wireOp",EDGE,"E13.0.1.1")}),1.0]])]});
            var Q15;
            Q15=makeQuery(id+"F2.imprint","IMPRINT",FACE,{"disambiguationData":[TD([[makeQuery(id+"F2.imprint","IMPRINT",EDGE,{"derivedFrom":sQuery(id+"F2.wireOp",EDGE,"E13.0.1.21")}),-1.0]])]});
            var Q16;
            Q16=makeQuery(id+"F2.imprint","IMPRINT",FACE,{"disambiguationData":[TD([[makeQuery(id+"F2.imprint","IMPRINT",EDGE,{"derivedFrom":sQuery(id+"F2.wireOp",EDGE,"E13.0.2.0")}),-1.0]])]});
            var Q17;
            Q17=makeQuery(id+"F2.imprint","IMPRINT",FACE,{"disambiguationData":[TD([[makeQuery(id+"F2.imprint","IMPRINT",EDGE,{"derivedFrom":sQuery(id+"F2.wireOp",EDGE,"E13.0.2.23")}),1.0]])]});
            var Q18;
            Q18=makeQuery(id+"F2.imprint","IMPRINT",FACE,{"disambiguationData":[TD([[makeQuery(id+"F2.imprint","IMPRINT",EDGE,{"derivedFrom":sQuery(id+"F2.wireOp",EDGE,"E13.0.2.2")}),-1.0]])]});
            var Q19;
            Q19=makeQuery(id+"F2.imprint","IMPRINT",FACE,{"disambiguationData":[TD([[makeQuery(id+"F2.imprint","IMPRINT",EDGE,{"derivedFrom":sQuery(id+"F2.wireOp",EDGE,"E13.0.2.7")}),1.0]])]});
            var Q20;
            Q20=makeQuery(id+"F2.imprint","IMPRINT",FACE,{"disambiguationData":[TD([[makeQuery(id+"F2.imprint","IMPRINT",EDGE,{"derivedFrom":sQuery(id+"F2.wireOp",EDGE,"E13.0.2.21")}),-1.0]])]});
            var Q21;
            Q21=makeQuery(id+"F2.imprint","IMPRINT",FACE,{"disambiguationData":[TD([[makeQuery(id+"F2.imprint","IMPRINT",EDGE,{"derivedFrom":sQuery(id+"F2.wireOp",EDGE,"E13.0.2.1")}),1.0]])]});
            var Q22;
            Q22=makeQuery(id+"F2.imprint","IMPRINT",FACE,{"disambiguationData":[TD([[makeQuery(id+"F2.imprint","IMPRINT",EDGE,{"derivedFrom":sQuery(id+"F2.wireOp",EDGE,"E13.0.2.16")}),1.0]])]});
            var Q23;
            Q23=makeQuery(id+"F2.imprint","IMPRINT",FACE,{"disambiguationData":[TD([[makeQuery(id+"F2.imprint","IMPRINT",EDGE,{"derivedFrom":sQuery(id+"F2.wireOp",EDGE,"E13.0.2.3")}),-1.0]])]});
            var Q24;
            Q24=makeQuery(id+"F2.imprint","IMPRINT",FACE,{"disambiguationData":[TD([[makeQuery(id+"F2.imprint","IMPRINT",EDGE,{"derivedFrom":sQuery(id+"F2.wireOp",EDGE,"E13.0.3.0")}),-1.0]])]});
            var Q25;
            Q25=makeQuery(id+"F2.imprint","IMPRINT",FACE,{"disambiguationData":[TD([[makeQuery(id+"F2.imprint","IMPRINT",EDGE,{"derivedFrom":sQuery(id+"F2.wireOp",EDGE,"E13.0.3.23")}),1.0]])]});
            var Q26;
            Q26=makeQuery(id+"F2.imprint","IMPRINT",FACE,{"disambiguationData":[TD([[makeQuery(id+"F2.imprint","IMPRINT",EDGE,{"derivedFrom":sQuery(id+"F2.wireOp",EDGE,"E13.0.3.2")}),-1.0]])]});
            var Q27;
            Q27=makeQuery(id+"F2.imprint","IMPRINT",FACE,{"disambiguationData":[TD([[makeQuery(id+"F2.imprint","IMPRINT",EDGE,{"derivedFrom":sQuery(id+"F2.wireOp",EDGE,"E13.0.3.7")}),1.0]])]});
            var Q28;
            Q28=makeQuery(id+"F2.imprint","IMPRINT",FACE,{"disambiguationData":[TD([[makeQuery(id+"F2.imprint","IMPRINT",EDGE,{"derivedFrom":sQuery(id+"F2.wireOp",EDGE,"E13.0.3.16")}),1.0]])]});
            var Q29;
            Q29=makeQuery(id+"F2.imprint","IMPRINT",FACE,{"disambiguationData":[TD([[makeQuery(id+"F2.imprint","IMPRINT",EDGE,{"derivedFrom":sQuery(id+"F2.wireOp",EDGE,"E13.0.3.3")}),-1.0]])]});
            var Q30;
            Q30=makeQuery(id+"F2.imprint","IMPRINT",FACE,{"disambiguationData":[TD([[makeQuery(id+"F2.imprint","IMPRINT",EDGE,{"derivedFrom":sQuery(id+"F2.wireOp",EDGE,"E13.0.3.1")}),1.0]])]});
            var Q31;
            Q31=makeQuery(id+"F2.imprint","IMPRINT",FACE,{"disambiguationData":[TD([[makeQuery(id+"F2.imprint","IMPRINT",EDGE,{"derivedFrom":sQuery(id+"F2.wireOp",EDGE,"E13.0.3.21")}),-1.0]])]});
            var Q32;
            Q32=makeQuery(id+"F2.imprint","IMPRINT",FACE,{"disambiguationData":[TD([[makeQuery(id+"F2.imprint","IMPRINT",EDGE,{"derivedFrom":sQuery(id+"F2.wireOp",EDGE,"E14.0.1.11")}),-1.0]])]});
            var Q33;
            Q33=makeQuery(id+"F2.imprint","IMPRINT",FACE,{"disambiguationData":[TD([[makeQuery(id+"F2.imprint","IMPRINT",EDGE,{"derivedFrom":sQuery(id+"F2.wireOp",EDGE,"E14.0.1.13")}),1.0]])]});
            var Q34;
            Q34=makeQuery(id+"F2.imprint","IMPRINT",FACE,{"disambiguationData":[TD([[makeQuery(id+"F2.imprint","IMPRINT",EDGE,{"derivedFrom":sQuery(id+"F2.wireOp",EDGE,"E14.0.1.9")}),-1.0]])]});
            var Q35;
            Q35=makeQuery(id+"F2.imprint","IMPRINT",FACE,{"disambiguationData":[TD([[makeQuery(id+"F2.imprint","IMPRINT",EDGE,{"derivedFrom":sQuery(id+"F2.wireOp",EDGE,"E14.0.1.0")}),-1.0]])]});
            extrude(context, id + "F3", {"entities" : qUnion([Q0, Q1, Q2, Q3, Q4, Q5, Q6, Q7, Q8, Q9, Q10, Q11, Q12, Q13, Q14, Q15, Q16, Q17, Q18, Q19, Q20, Q21, Q22, Q23, Q24, Q25, Q26, Q27, Q28, Q29, Q30, Q31, Q32, Q33, Q34, Q35]), "operationType" : NewBodyOperationType.ADD, "depth" : 0.5 * mm, "offsetDistance" : 25 * mm, "hasSecondDirection" : true, "secondDirectionOppositeDirection" : true, "secondDirectionDepth" : 20.5 * mm});
        }
        {
            var Q0;
            {var subQ0=sQuery(id+"F0.wireOp",EDGE,"E0.right");var subQ1=makeQuery(id+"F1.opExtrude","CAP_EDGE",EDGE,{"disambiguationData":[OSD([subQ0])],"isStart":false});Q0=makeQuery(id+"F3.boolean.opBoolean","MERGE",FACE,{"derivedFrom":[makeQuery(id+"F1.opExtrude","SWEPT_FACE",FACE,{"disambiguationData":[OSD([subQ0])]}),makeQuery(id+"F3.opExtrude","SWEPT_FACE",FACE,{"disambiguationData":[OSD([sQuery(id+"F2.wireOp",EDGE,"E1.left")])]}),makeQuery(id+"F3.opExtrude","SWEPT_FACE",FACE,{"disambiguationData":[OSD([sQuery(id+"F2.wireOp",EDGE,"E13.0.1.9")])]}),makeQuery(id+"F3.opExtrude","SWEPT_FACE",FACE,{"disambiguationData":[OSD([sQuery(id+"F2.wireOp",EDGE,"E13.0.2.9")])]}),makeQuery(id+"F3.opExtrude","SWEPT_FACE",FACE,{"disambiguationData":[OSD([sQuery(id+"F2.wireOp",EDGE,"E13.0.3.9")])]}),makeQuery(id+"F3.opExtrude","SWEPT_FACE",FACE,{"disambiguationData":[OSD([sQuery(id+"F2.wireOp",EDGE,"E14.0.1.17")])]}),makeQuery(id+"F3.opExtrude","SWEPT_FACE",FACE,{"disambiguationData":[OSD([subQ0]),TDD([makeQuery(id+"F2.imprint","IMPRINT",EDGE,{"disambiguationData":[TD([[makeQuery(id+"F2.imprint","INTERSECT",VERTEX,{"derivedFrom":[subQ1,sQuery(id+"F2.wireOp",EDGE,"E12.3.0.3")]}),-1.0]])],"derivedFrom":subQ1})])]}),makeQuery(id+"F3.opExtrude","SWEPT_FACE",FACE,{"disambiguationData":[OSD([subQ0]),TDD([makeQuery(id+"F2.imprint","IMPRINT",EDGE,{"disambiguationData":[TD([[makeQuery(id+"F2.imprint","INTERSECT",VERTEX,{"derivedFrom":[subQ1,sQuery(id+"F2.wireOp",EDGE,"E13.0.1.33")]}),1.0]])],"derivedFrom":subQ1})])]}),makeQuery(id+"F3.opExtrude","SWEPT_FACE",FACE,{"disambiguationData":[OSD([subQ0]),TDD([makeQuery(id+"F2.imprint","IMPRINT",EDGE,{"disambiguationData":[TD([[makeQuery(id+"F2.imprint","INTERSECT",VERTEX,{"derivedFrom":[subQ1,sQuery(id+"F2.wireOp",EDGE,"E13.0.2.33")]}),1.0]])],"derivedFrom":subQ1})])]}),makeQuery(id+"F3.opExtrude","SWEPT_FACE",FACE,{"disambiguationData":[OSD([subQ0]),TDD([makeQuery(id+"F2.imprint","IMPRINT",EDGE,{"disambiguationData":[TD([[makeQuery(id+"F2.imprint","INTERSECT",VERTEX,{"derivedFrom":[subQ1,sQuery(id+"F2.wireOp",EDGE,"E13.0.3.33")]}),1.0]])],"derivedFrom":subQ1})])]})]});}
            var sketch = newSketch(context, id + "F4", { "sketchPlane" : qUnion([Q0])});
            skLineSegment(sketch, "E15.bottom", {"start": v(-10.51, 36.84) * mm, "end": v(-0.51, 36.84) * mm});
            skLineSegment(sketch, "E15.top", {"start": v(-10.51, 26.84) * mm, "end": v(-1.01, 26.84) * mm});
            skLineSegment(sketch, "E15.left", {"start": v(-10.51, 36.84) * mm, "end": v(-10.51, 26.84) * mm});
            skLineSegment(sketch, "E15.right", {"start": v(-0.51, 36.34) * mm, "end": v(-0.51, 27.34) * mm});
            skLineSegment(sketch, "E16.1.0.0", {"start": v(0.99, 36.84) * mm, "end": v(10.49, 36.84) * mm});
            skLineSegment(sketch, "E16.1.0.1", {"start": v(0.49, 36.34) * mm, "end": v(0.49, 27.34) * mm});
            skLineSegment(sketch, "E16.1.0.2", {"start": v(0.99, 26.84) * mm, "end": v(10.49, 26.84) * mm});
            skLineSegment(sketch, "E16.1.0.3", {"start": v(10.49, 36.84) * mm, "end": v(10.49, 26.84) * mm});
            skLineSegment(sketch, "E16.direction1", {"start": v(-10.51, 36.84) * mm, "end": v(-1.01, 36.84) * mm, "construction": true});
            skPoint(sketch, "E17.visualSharp", {"position": v(-0.51, 26.84) * mm});
            skArc(sketch, "E17.filletArc", {"start": v(-1.01, 26.84) * mm, "mid": v(-0.66, 26.99) * mm, "end": v(-0.51, 27.34) * mm});
            skPoint(sketch, "E18.newPointA", {"position": v(0.49, 36.84) * mm});
            skPoint(sketch, "E18.newPointB", {"position": v(-0.51, 36.84) * mm});
            skArc(sketch, "E18.filletArc", {"start": v(-0.51, 36.34) * mm, "mid": v(-0.66, 36.7) * mm, "end": v(-1.01, 36.84) * mm});
            skArc(sketch, "E19.filletArc", {"start": v(0.99, 36.84) * mm, "mid": v(0.64, 36.7) * mm, "end": v(0.49, 36.34) * mm});
            skPoint(sketch, "E20.visualSharp", {"position": v(0.49, 26.84) * mm});
            skArc(sketch, "E20.filletArc", {"start": v(0.49, 27.34) * mm, "mid": v(0.64, 26.99) * mm, "end": v(0.99, 26.84) * mm});
            skPoint(sketch, "E21.0.1.0", {"position": v(0.49, 25.84) * mm});
            skLineSegment(sketch, "E21.0.1.1", {"start": v(-10.51, 25.84) * mm, "end": v(-1.01, 25.84) * mm, "construction": true});
            skLineSegment(sketch, "E21.0.1.2", {"start": v(10.49, 25.84) * mm, "end": v(10.49, 15.84) * mm});
            skLineSegment(sketch, "E21.0.1.3", {"start": v(0.99, 15.84) * mm, "end": v(10.49, 15.84) * mm});
            skLineSegment(sketch, "E21.0.1.4", {"start": v(0.49, 25.34) * mm, "end": v(0.49, 16.34) * mm});
            skLineSegment(sketch, "E21.0.1.5", {"start": v(0.99, 25.84) * mm, "end": v(10.49, 25.84) * mm});
            skLineSegment(sketch, "E21.0.1.6", {"start": v(-0.51, 25.34) * mm, "end": v(-0.51, 16.34) * mm});
            skLineSegment(sketch, "E21.0.1.7", {"start": v(-10.51, 25.84) * mm, "end": v(-10.51, 15.84) * mm});
            skLineSegment(sketch, "E21.0.1.8", {"start": v(-10.51, 15.84) * mm, "end": v(-1.01, 15.84) * mm});
            skPoint(sketch, "E21.0.1.9", {"position": v(-0.51, 25.84) * mm});
            skPoint(sketch, "E21.0.1.10", {"position": v(-0.51, 15.84) * mm});
            skPoint(sketch, "E21.0.1.11", {"position": v(0.49, 15.84) * mm});
            skPoint(sketch, "E21.0.1.12", {"position": v(0.49, 25.84) * mm});
            skLineSegment(sketch, "E21.0.1.13", {"start": v(-10.51, 25.84) * mm, "end": v(-0.51, 25.84) * mm});
            skArc(sketch, "E21.0.1.14", {"start": v(0.49, 16.34) * mm, "mid": v(0.64, 15.99) * mm, "end": v(0.99, 15.84) * mm});
            skArc(sketch, "E21.0.1.15", {"start": v(-0.51, 25.34) * mm, "mid": v(-0.66, 25.7) * mm, "end": v(-1.01, 25.84) * mm});
            skArc(sketch, "E21.0.1.16", {"start": v(-1.01, 15.84) * mm, "mid": v(-0.66, 15.99) * mm, "end": v(-0.51, 16.34) * mm});
            skArc(sketch, "E21.0.1.17", {"start": v(0.99, 25.84) * mm, "mid": v(0.64, 25.7) * mm, "end": v(0.49, 25.34) * mm});
            skPoint(sketch, "E21.0.2.0", {"position": v(0.49, 14.84) * mm});
            skLineSegment(sketch, "E21.0.2.1", {"start": v(-10.51, 14.84) * mm, "end": v(-1.01, 14.84) * mm, "construction": true});
            skLineSegment(sketch, "E21.0.2.2", {"start": v(10.49, 14.84) * mm, "end": v(10.49, 4.84) * mm});
            skLineSegment(sketch, "E21.0.2.3", {"start": v(0.99, 4.84) * mm, "end": v(10.49, 4.84) * mm});
            skLineSegment(sketch, "E21.0.2.4", {"start": v(0.49, 14.34) * mm, "end": v(0.49, 5.34) * mm});
            skLineSegment(sketch, "E21.0.2.5", {"start": v(0.99, 14.84) * mm, "end": v(10.49, 14.84) * mm});
            skLineSegment(sketch, "E21.0.2.6", {"start": v(-0.51, 14.34) * mm, "end": v(-0.51, 5.34) * mm});
            skLineSegment(sketch, "E21.0.2.7", {"start": v(-10.51, 14.84) * mm, "end": v(-10.51, 4.84) * mm});
            skLineSegment(sketch, "E21.0.2.8", {"start": v(-10.51, 4.84) * mm, "end": v(-1.01, 4.84) * mm});
            skPoint(sketch, "E21.0.2.9", {"position": v(-0.51, 14.84) * mm});
            skPoint(sketch, "E21.0.2.10", {"position": v(-0.51, 4.84) * mm});
            skPoint(sketch, "E21.0.2.11", {"position": v(0.49, 4.84) * mm});
            skPoint(sketch, "E21.0.2.12", {"position": v(0.49, 14.84) * mm});
            skLineSegment(sketch, "E21.0.2.13", {"start": v(-10.51, 14.84) * mm, "end": v(-0.51, 14.84) * mm});
            skArc(sketch, "E21.0.2.14", {"start": v(0.49, 5.34) * mm, "mid": v(0.64, 4.99) * mm, "end": v(0.99, 4.84) * mm});
            skArc(sketch, "E21.0.2.15", {"start": v(-0.51, 14.34) * mm, "mid": v(-0.66, 14.7) * mm, "end": v(-1.01, 14.84) * mm});
            skArc(sketch, "E21.0.2.16", {"start": v(-1.01, 4.84) * mm, "mid": v(-0.66, 4.99) * mm, "end": v(-0.51, 5.34) * mm});
            skArc(sketch, "E21.0.2.17", {"start": v(0.99, 14.84) * mm, "mid": v(0.64, 14.7) * mm, "end": v(0.49, 14.34) * mm});
            skPoint(sketch, "E21.0.3.0", {"position": v(0.49, 3.84) * mm});
            skLineSegment(sketch, "E21.0.3.1", {"start": v(-10.51, 3.84) * mm, "end": v(-1.01, 3.84) * mm, "construction": true});
            skLineSegment(sketch, "E21.0.3.2", {"start": v(10.49, 3.84) * mm, "end": v(10.49, -6.16) * mm});
            skLineSegment(sketch, "E21.0.3.3", {"start": v(0.99, -6.16) * mm, "end": v(10.49, -6.16) * mm});
            skLineSegment(sketch, "E21.0.3.4", {"start": v(0.49, 3.34) * mm, "end": v(0.49, -5.66) * mm});
            skLineSegment(sketch, "E21.0.3.5", {"start": v(0.99, 3.84) * mm, "end": v(10.49, 3.84) * mm});
            skLineSegment(sketch, "E21.0.3.6", {"start": v(-0.51, 3.34) * mm, "end": v(-0.51, -5.66) * mm});
            skLineSegment(sketch, "E21.0.3.7", {"start": v(-10.51, 3.84) * mm, "end": v(-10.51, -6.16) * mm});
            skLineSegment(sketch, "E21.0.3.8", {"start": v(-10.51, -6.16) * mm, "end": v(-1.01, -6.16) * mm});
            skPoint(sketch, "E21.0.3.9", {"position": v(-0.51, 3.84) * mm});
            skPoint(sketch, "E21.0.3.10", {"position": v(-0.51, -6.16) * mm});
            skPoint(sketch, "E21.0.3.11", {"position": v(0.49, -6.16) * mm});
            skPoint(sketch, "E21.0.3.12", {"position": v(0.49, 3.84) * mm});
            skLineSegment(sketch, "E21.0.3.13", {"start": v(-10.51, 3.84) * mm, "end": v(-0.51, 3.84) * mm});
            skArc(sketch, "E21.0.3.14", {"start": v(0.49, -5.66) * mm, "mid": v(0.64, -6.01) * mm, "end": v(0.99, -6.16) * mm});
            skArc(sketch, "E21.0.3.15", {"start": v(-0.51, 3.34) * mm, "mid": v(-0.66, 3.7) * mm, "end": v(-1.01, 3.84) * mm});
            skArc(sketch, "E21.0.3.16", {"start": v(-1.01, -6.16) * mm, "mid": v(-0.66, -6.01) * mm, "end": v(-0.51, -5.66) * mm});
            skArc(sketch, "E21.0.3.17", {"start": v(0.99, 3.84) * mm, "mid": v(0.64, 3.7) * mm, "end": v(0.49, 3.34) * mm});
            skPoint(sketch, "E21.0.4.0", {"position": v(0.49, -7.16) * mm});
            skLineSegment(sketch, "E21.0.4.1", {"start": v(-10.51, -7.16) * mm, "end": v(-1.01, -7.16) * mm, "construction": true});
            skLineSegment(sketch, "E21.0.4.2", {"start": v(10.49, -7.16) * mm, "end": v(10.49, -17.16) * mm});
            skLineSegment(sketch, "E21.0.4.3", {"start": v(0.99, -17.16) * mm, "end": v(10.49, -17.16) * mm});
            skLineSegment(sketch, "E21.0.4.4", {"start": v(0.49, -7.66) * mm, "end": v(0.49, -16.66) * mm});
            skLineSegment(sketch, "E21.0.4.5", {"start": v(0.99, -7.16) * mm, "end": v(10.49, -7.16) * mm});
            skLineSegment(sketch, "E21.0.4.6", {"start": v(-0.51, -7.66) * mm, "end": v(-0.51, -16.66) * mm});
            skLineSegment(sketch, "E21.0.4.7", {"start": v(-10.51, -7.16) * mm, "end": v(-10.51, -17.16) * mm});
            skLineSegment(sketch, "E21.0.4.8", {"start": v(-10.51, -17.16) * mm, "end": v(-1.01, -17.16) * mm});
            skPoint(sketch, "E21.0.4.9", {"position": v(-0.51, -7.16) * mm});
            skPoint(sketch, "E21.0.4.10", {"position": v(-0.51, -17.16) * mm});
            skPoint(sketch, "E21.0.4.11", {"position": v(0.49, -17.16) * mm});
            skPoint(sketch, "E21.0.4.12", {"position": v(0.49, -7.16) * mm});
            skLineSegment(sketch, "E21.0.4.13", {"start": v(-10.51, -7.16) * mm, "end": v(-0.51, -7.16) * mm});
            skArc(sketch, "E21.0.4.14", {"start": v(0.49, -16.66) * mm, "mid": v(0.64, -17.01) * mm, "end": v(0.99, -17.16) * mm});
            skArc(sketch, "E21.0.4.15", {"start": v(-0.51, -7.66) * mm, "mid": v(-0.66, -7.3) * mm, "end": v(-1.01, -7.16) * mm});
            skArc(sketch, "E21.0.4.16", {"start": v(-1.01, -17.16) * mm, "mid": v(-0.66, -17.01) * mm, "end": v(-0.51, -16.66) * mm});
            skArc(sketch, "E21.0.4.17", {"start": v(0.99, -7.16) * mm, "mid": v(0.64, -7.3) * mm, "end": v(0.49, -7.66) * mm});
            skPoint(sketch, "E21.0.5.0", {"position": v(0.49, -18.16) * mm});
            skLineSegment(sketch, "E21.0.5.1", {"start": v(-10.51, -18.16) * mm, "end": v(-1.01, -18.16) * mm, "construction": true});
            skLineSegment(sketch, "E21.0.5.2", {"start": v(10.49, -18.16) * mm, "end": v(10.49, -28.16) * mm});
            skLineSegment(sketch, "E21.0.5.3", {"start": v(0.99, -28.16) * mm, "end": v(10.49, -28.16) * mm});
            skLineSegment(sketch, "E21.0.5.4", {"start": v(0.49, -18.66) * mm, "end": v(0.49, -27.66) * mm});
            skLineSegment(sketch, "E21.0.5.5", {"start": v(0.99, -18.16) * mm, "end": v(10.49, -18.16) * mm});
            skLineSegment(sketch, "E21.0.5.6", {"start": v(-0.51, -18.66) * mm, "end": v(-0.51, -27.66) * mm});
            skLineSegment(sketch, "E21.0.5.7", {"start": v(-10.51, -18.16) * mm, "end": v(-10.51, -28.16) * mm});
            skLineSegment(sketch, "E21.0.5.8", {"start": v(-10.51, -28.16) * mm, "end": v(-1.01, -28.16) * mm});
            skPoint(sketch, "E21.0.5.9", {"position": v(-0.51, -18.16) * mm});
            skPoint(sketch, "E21.0.5.10", {"position": v(-0.51, -28.16) * mm});
            skPoint(sketch, "E21.0.5.11", {"position": v(0.49, -28.16) * mm});
            skPoint(sketch, "E21.0.5.12", {"position": v(0.49, -18.16) * mm});
            skLineSegment(sketch, "E21.0.5.13", {"start": v(-10.51, -18.16) * mm, "end": v(-0.51, -18.16) * mm});
            skArc(sketch, "E21.0.5.14", {"start": v(0.49, -27.66) * mm, "mid": v(0.64, -28.01) * mm, "end": v(0.99, -28.16) * mm});
            skArc(sketch, "E21.0.5.15", {"start": v(-0.51, -18.66) * mm, "mid": v(-0.66, -18.3) * mm, "end": v(-1.01, -18.16) * mm});
            skArc(sketch, "E21.0.5.16", {"start": v(-1.01, -28.16) * mm, "mid": v(-0.66, -28.01) * mm, "end": v(-0.51, -27.66) * mm});
            skArc(sketch, "E21.0.5.17", {"start": v(0.99, -18.16) * mm, "mid": v(0.64, -18.3) * mm, "end": v(0.49, -18.66) * mm});
            skPoint(sketch, "E21.0.6.0", {"position": v(0.49, -29.16) * mm});
            skLineSegment(sketch, "E21.0.6.1", {"start": v(-10.51, -29.16) * mm, "end": v(-1.01, -29.16) * mm, "construction": true});
            skLineSegment(sketch, "E21.0.6.2", {"start": v(10.49, -29.16) * mm, "end": v(10.49, -39.16) * mm});
            skLineSegment(sketch, "E21.0.6.3", {"start": v(0.99, -39.16) * mm, "end": v(10.49, -39.16) * mm});
            skLineSegment(sketch, "E21.0.6.4", {"start": v(0.49, -29.66) * mm, "end": v(0.49, -38.66) * mm});
            skLineSegment(sketch, "E21.0.6.5", {"start": v(0.99, -29.16) * mm, "end": v(10.49, -29.16) * mm});
            skLineSegment(sketch, "E21.0.6.6", {"start": v(-0.51, -29.66) * mm, "end": v(-0.51, -38.66) * mm});
            skLineSegment(sketch, "E21.0.6.7", {"start": v(-10.51, -29.16) * mm, "end": v(-10.51, -39.16) * mm});
            skLineSegment(sketch, "E21.0.6.8", {"start": v(-10.51, -39.16) * mm, "end": v(-1.01, -39.16) * mm});
            skPoint(sketch, "E21.0.6.9", {"position": v(-0.51, -29.16) * mm});
            skPoint(sketch, "E21.0.6.10", {"position": v(-0.51, -39.16) * mm});
            skPoint(sketch, "E21.0.6.11", {"position": v(0.49, -39.16) * mm});
            skPoint(sketch, "E21.0.6.12", {"position": v(0.49, -29.16) * mm});
            skLineSegment(sketch, "E21.0.6.13", {"start": v(-10.51, -29.16) * mm, "end": v(-0.51, -29.16) * mm});
            skArc(sketch, "E21.0.6.14", {"start": v(0.49, -38.66) * mm, "mid": v(0.64, -39.01) * mm, "end": v(0.99, -39.16) * mm});
            skArc(sketch, "E21.0.6.15", {"start": v(-0.51, -29.66) * mm, "mid": v(-0.66, -29.3) * mm, "end": v(-1.01, -29.16) * mm});
            skArc(sketch, "E21.0.6.16", {"start": v(-1.01, -39.16) * mm, "mid": v(-0.66, -39.01) * mm, "end": v(-0.51, -38.66) * mm});
            skArc(sketch, "E21.0.6.17", {"start": v(0.99, -29.16) * mm, "mid": v(0.64, -29.3) * mm, "end": v(0.49, -29.66) * mm});
            skPoint(sketch, "E21.0.7.0", {"position": v(0.49, -40.16) * mm});
            skLineSegment(sketch, "E21.0.7.1", {"start": v(-10.51, -40.16) * mm, "end": v(-1.01, -40.16) * mm, "construction": true});
            skLineSegment(sketch, "E21.0.7.2", {"start": v(10.49, -40.16) * mm, "end": v(10.49, -50.16) * mm});
            skLineSegment(sketch, "E21.0.7.3", {"start": v(0.99, -50.16) * mm, "end": v(10.49, -50.16) * mm});
            skLineSegment(sketch, "E21.0.7.4", {"start": v(0.49, -40.66) * mm, "end": v(0.49, -49.66) * mm});
            skLineSegment(sketch, "E21.0.7.5", {"start": v(0.99, -40.16) * mm, "end": v(10.49, -40.16) * mm});
            skLineSegment(sketch, "E21.0.7.6", {"start": v(-0.51, -40.66) * mm, "end": v(-0.51, -49.66) * mm});
            skLineSegment(sketch, "E21.0.7.7", {"start": v(-10.51, -40.16) * mm, "end": v(-10.51, -50.16) * mm});
            skLineSegment(sketch, "E21.0.7.8", {"start": v(-10.51, -50.16) * mm, "end": v(-1.01, -50.16) * mm});
            skPoint(sketch, "E21.0.7.9", {"position": v(-0.51, -40.16) * mm});
            skPoint(sketch, "E21.0.7.10", {"position": v(-0.51, -50.16) * mm});
            skPoint(sketch, "E21.0.7.11", {"position": v(0.49, -50.16) * mm});
            skPoint(sketch, "E21.0.7.12", {"position": v(0.49, -40.16) * mm});
            skLineSegment(sketch, "E21.0.7.13", {"start": v(-10.51, -40.16) * mm, "end": v(-0.51, -40.16) * mm});
            skArc(sketch, "E21.0.7.14", {"start": v(0.49, -49.66) * mm, "mid": v(0.64, -50.01) * mm, "end": v(0.99, -50.16) * mm});
            skArc(sketch, "E21.0.7.15", {"start": v(-0.51, -40.66) * mm, "mid": v(-0.66, -40.3) * mm, "end": v(-1.01, -40.16) * mm});
            skArc(sketch, "E21.0.7.16", {"start": v(-1.01, -50.16) * mm, "mid": v(-0.66, -50.01) * mm, "end": v(-0.51, -49.66) * mm});
            skArc(sketch, "E21.0.7.17", {"start": v(0.99, -40.16) * mm, "mid": v(0.64, -40.3) * mm, "end": v(0.49, -40.66) * mm});
            skPoint(sketch, "E21.0.8.0", {"position": v(0.49, -51.16) * mm});
            skLineSegment(sketch, "E21.0.8.1", {"start": v(-10.51, -51.16) * mm, "end": v(-1.01, -51.16) * mm, "construction": true});
            skLineSegment(sketch, "E21.0.8.2", {"start": v(10.49, -51.16) * mm, "end": v(10.49, -61.16) * mm});
            skLineSegment(sketch, "E21.0.8.3", {"start": v(0.99, -61.16) * mm, "end": v(10.49, -61.16) * mm});
            skLineSegment(sketch, "E21.0.8.4", {"start": v(0.49, -51.66) * mm, "end": v(0.49, -60.66) * mm});
            skLineSegment(sketch, "E21.0.8.5", {"start": v(0.99, -51.16) * mm, "end": v(10.49, -51.16) * mm});
            skLineSegment(sketch, "E21.0.8.6", {"start": v(-0.51, -51.66) * mm, "end": v(-0.51, -60.66) * mm});
            skLineSegment(sketch, "E21.0.8.7", {"start": v(-10.51, -51.16) * mm, "end": v(-10.51, -61.16) * mm});
            skLineSegment(sketch, "E21.0.8.8", {"start": v(-10.51, -61.16) * mm, "end": v(-1.01, -61.16) * mm});
            skPoint(sketch, "E21.0.8.9", {"position": v(-0.51, -51.16) * mm});
            skPoint(sketch, "E21.0.8.10", {"position": v(-0.51, -61.16) * mm});
            skPoint(sketch, "E21.0.8.11", {"position": v(0.49, -61.16) * mm});
            skPoint(sketch, "E21.0.8.12", {"position": v(0.49, -51.16) * mm});
            skLineSegment(sketch, "E21.0.8.13", {"start": v(-10.51, -51.16) * mm, "end": v(-0.51, -51.16) * mm});
            skArc(sketch, "E21.0.8.14", {"start": v(0.49, -60.66) * mm, "mid": v(0.64, -61.01) * mm, "end": v(0.99, -61.16) * mm});
            skArc(sketch, "E21.0.8.15", {"start": v(-0.51, -51.66) * mm, "mid": v(-0.66, -51.3) * mm, "end": v(-1.01, -51.16) * mm});
            skArc(sketch, "E21.0.8.16", {"start": v(-1.01, -61.16) * mm, "mid": v(-0.66, -61.01) * mm, "end": v(-0.51, -60.66) * mm});
            skArc(sketch, "E21.0.8.17", {"start": v(0.99, -51.16) * mm, "mid": v(0.64, -51.3) * mm, "end": v(0.49, -51.66) * mm});
            skLineSegment(sketch, "E21.direction1", {"start": v(-10.51, 26.84) * mm, "end": v(14.49, 26.84) * mm, "construction": true});
            skLineSegment(sketch, "E21.direction2", {"start": v(-10.51, 26.84) * mm, "end": v(-10.51, 15.84) * mm, "construction": true});
            skSolve(sketch);
        }
        {
            var Q0;
            Q0=makeQuery(id+"F4.imprint","IMPRINT",FACE,{"disambiguationData":[TD([[makeQuery(id+"F4.imprint","IMPRINT",EDGE,{"derivedFrom":sQuery(id+"F4.wireOp",EDGE,"E21.0.8.6")}),-1.0]])]});
            var Q1;
            Q1=makeQuery(id+"F4.imprint","IMPRINT",FACE,{"disambiguationData":[TD([[makeQuery(id+"F4.imprint","IMPRINT",EDGE,{"derivedFrom":sQuery(id+"F4.wireOp",EDGE,"E21.0.8.4")}),1.0]])]});
            var Q2;
            {var subQ20=sQuery(id+"F4.wireOp",EDGE,"E21.0.7.2");Q2=makeQuery(id+"F4.imprint","IMPRINT",FACE,{"disambiguationData":[TD([[makeQuery(id+"F4.imprint","IMPRINT",EDGE,{"derivedFrom":subQ20}),-1.0]])]});}
            var Q3;
            Q3=makeQuery(id+"F4.imprint","IMPRINT",FACE,{"disambiguationData":[TD([[makeQuery(id+"F4.imprint","IMPRINT",EDGE,{"derivedFrom":sQuery(id+"F4.wireOp",EDGE,"E21.0.7.6")}),-1.0]])]});
            var Q4;
            Q4=makeQuery(id+"F4.imprint","IMPRINT",FACE,{"disambiguationData":[TD([[makeQuery(id+"F4.imprint","IMPRINT",EDGE,{"derivedFrom":sQuery(id+"F4.wireOp",EDGE,"E21.0.6.6")}),-1.0]])]});
            var Q5;
            Q5=makeQuery(id+"F4.imprint","IMPRINT",FACE,{"disambiguationData":[TD([[makeQuery(id+"F4.imprint","IMPRINT",EDGE,{"derivedFrom":sQuery(id+"F4.wireOp",EDGE,"E21.0.6.4")}),1.0]])]});
            var Q6;
            {var subQ20=sQuery(id+"F4.wireOp",EDGE,"E21.0.5.2");Q6=makeQuery(id+"F4.imprint","IMPRINT",FACE,{"disambiguationData":[TD([[makeQuery(id+"F4.imprint","IMPRINT",EDGE,{"derivedFrom":subQ20}),-1.0]])]});}
            var Q7;
            Q7=makeQuery(id+"F4.imprint","IMPRINT",FACE,{"disambiguationData":[TD([[makeQuery(id+"F4.imprint","IMPRINT",EDGE,{"derivedFrom":sQuery(id+"F4.wireOp",EDGE,"E21.0.5.6")}),-1.0]])]});
            var Q8;
            Q8=makeQuery(id+"F4.imprint","IMPRINT",FACE,{"disambiguationData":[TD([[makeQuery(id+"F4.imprint","IMPRINT",EDGE,{"derivedFrom":sQuery(id+"F4.wireOp",EDGE,"E21.0.4.6")}),-1.0]])]});
            var Q9;
            Q9=makeQuery(id+"F4.imprint","IMPRINT",FACE,{"disambiguationData":[TD([[makeQuery(id+"F4.imprint","IMPRINT",EDGE,{"derivedFrom":sQuery(id+"F4.wireOp",EDGE,"E21.0.4.4")}),1.0]])]});
            var Q10;
            {var subQ20=sQuery(id+"F4.wireOp",EDGE,"E21.0.3.2");Q10=makeQuery(id+"F4.imprint","IMPRINT",FACE,{"disambiguationData":[TD([[makeQuery(id+"F4.imprint","IMPRINT",EDGE,{"derivedFrom":subQ20}),-1.0]])]});}
            var Q11;
            Q11=makeQuery(id+"F4.imprint","IMPRINT",FACE,{"disambiguationData":[TD([[makeQuery(id+"F4.imprint","IMPRINT",EDGE,{"derivedFrom":sQuery(id+"F4.wireOp",EDGE,"E21.0.3.6")}),-1.0]])]});
            var Q12;
            Q12=makeQuery(id+"F4.imprint","IMPRINT",FACE,{"disambiguationData":[TD([[makeQuery(id+"F4.imprint","IMPRINT",EDGE,{"derivedFrom":sQuery(id+"F4.wireOp",EDGE,"E21.0.2.6")}),-1.0]])]});
            var Q13;
            Q13=makeQuery(id+"F4.imprint","IMPRINT",FACE,{"disambiguationData":[TD([[makeQuery(id+"F4.imprint","IMPRINT",EDGE,{"derivedFrom":sQuery(id+"F4.wireOp",EDGE,"E21.0.2.4")}),1.0]])]});
            var Q14;
            Q14=makeQuery(id+"F4.imprint","IMPRINT",FACE,{"disambiguationData":[TD([[makeQuery(id+"F4.imprint","IMPRINT",EDGE,{"derivedFrom":sQuery(id+"F4.wireOp",EDGE,"E21.0.1.6")}),-1.0]])]});
            var Q15;
            {var subQ20=sQuery(id+"F4.wireOp",EDGE,"E21.0.1.2");Q15=makeQuery(id+"F4.imprint","IMPRINT",FACE,{"disambiguationData":[TD([[makeQuery(id+"F4.imprint","IMPRINT",EDGE,{"derivedFrom":subQ20}),-1.0]])]});}
            var Q16;
            Q16=makeQuery(id+"F4.imprint","IMPRINT",FACE,{"disambiguationData":[TD([[makeQuery(id+"F4.imprint","IMPRINT",EDGE,{"derivedFrom":sQuery(id+"F4.wireOp",EDGE,"E16.1.0.1")}),1.0]])]});
            var Q17;
            Q17=makeQuery(id+"F4.imprint","IMPRINT",FACE,{"disambiguationData":[TD([[makeQuery(id+"F4.imprint","IMPRINT",EDGE,{"derivedFrom":sQuery(id+"F4.wireOp",EDGE,"E15.right")}),-1.0]])]});
            extrude(context, id + "F5", {"entities" : qUnion([Q0, Q1, Q2, Q3, Q4, Q5, Q6, Q7, Q8, Q9, Q10, Q11, Q12, Q13, Q14, Q15, Q16, Q17]), "operationType" : NewBodyOperationType.ADD, "depth" : 0.5 * mm, "offsetDistance" : 25 * mm, "hasSecondDirection" : true, "secondDirectionOppositeDirection" : true, "secondDirectionDepth" : 0.5 * mm});
        }
        {
            var Q0;
            {var subQ0=sQuery(id+"F0.wireOp",EDGE,"E0.left");var subQ1=makeQuery(id+"F1.opExtrude","CAP_EDGE",EDGE,{"disambiguationData":[OSD([subQ0])],"isStart":false});Q0=makeQuery(id+"F3.boolean.opBoolean","MERGE",FACE,{"derivedFrom":[makeQuery(id+"F1.opExtrude","SWEPT_FACE",FACE,{"disambiguationData":[OSD([subQ0])]}),makeQuery(id+"F3.opExtrude","SWEPT_FACE",FACE,{"disambiguationData":[OSD([sQuery(id+"F2.wireOp",EDGE,"E7.left")])]}),makeQuery(id+"F3.opExtrude","SWEPT_FACE",FACE,{"disambiguationData":[OSD([sQuery(id+"F2.wireOp",EDGE,"E13.0.1.24")])]}),makeQuery(id+"F3.opExtrude","SWEPT_FACE",FACE,{"disambiguationData":[OSD([sQuery(id+"F2.wireOp",EDGE,"E13.0.2.24")])]}),makeQuery(id+"F3.opExtrude","SWEPT_FACE",FACE,{"disambiguationData":[OSD([sQuery(id+"F2.wireOp",EDGE,"E13.0.3.24")])]}),makeQuery(id+"F3.opExtrude","SWEPT_FACE",FACE,{"disambiguationData":[OSD([subQ0]),TDD([makeQuery(id+"F2.imprint","IMPRINT",EDGE,{"disambiguationData":[TD([[makeQuery(id+"F2.imprint","INTERSECT",VERTEX,{"derivedFrom":[subQ1,sQuery(id+"F2.wireOp",EDGE,"E6.3.0.3")]}),-1.0]])],"derivedFrom":subQ1})])]}),makeQuery(id+"F3.opExtrude","SWEPT_FACE",FACE,{"disambiguationData":[OSD([subQ0]),TDD([makeQuery(id+"F2.imprint","IMPRINT",EDGE,{"disambiguationData":[TD([[makeQuery(id+"F2.imprint","INTERSECT",VERTEX,{"derivedFrom":[subQ1,sQuery(id+"F2.wireOp",EDGE,"E13.0.1.17")]}),1.0]])],"derivedFrom":subQ1})])]}),makeQuery(id+"F3.opExtrude","SWEPT_FACE",FACE,{"disambiguationData":[OSD([subQ0]),TDD([makeQuery(id+"F2.imprint","IMPRINT",EDGE,{"disambiguationData":[TD([[makeQuery(id+"F2.imprint","INTERSECT",VERTEX,{"derivedFrom":[subQ1,sQuery(id+"F2.wireOp",EDGE,"E13.0.2.17")]}),1.0]])],"derivedFrom":subQ1})])]}),makeQuery(id+"F3.opExtrude","SWEPT_FACE",FACE,{"disambiguationData":[OSD([subQ0]),TDD([makeQuery(id+"F2.imprint","IMPRINT",EDGE,{"disambiguationData":[TD([[makeQuery(id+"F2.imprint","INTERSECT",VERTEX,{"derivedFrom":[subQ1,sQuery(id+"F2.wireOp",EDGE,"E13.0.3.17")]}),1.0]])],"derivedFrom":subQ1})])]}),makeQuery(id+"F3.opExtrude","SWEPT_FACE",FACE,{"disambiguationData":[OSD([subQ0]),TDD([makeQuery(id+"F2.imprint","IMPRINT",EDGE,{"disambiguationData":[TD([[makeQuery(id+"F2.imprint","INTERSECT",VERTEX,{"derivedFrom":[subQ1,sQuery(id+"F2.wireOp",EDGE,"E14.0.1.2")]}),1.0]])],"derivedFrom":subQ1})])]})]});}
            var sketch = newSketch(context, id + "F6", { "sketchPlane" : qUnion([Q0])});
            skLineSegment(sketch, "E22.bottom", {"start": v(-10.5, 36.84) * mm, "end": v(-0.5, 36.84) * mm});
            skLineSegment(sketch, "E22.top", {"start": v(-10.5, 26.84) * mm, "end": v(-1, 26.84) * mm});
            skLineSegment(sketch, "E22.left", {"start": v(-10.5, 36.84) * mm, "end": v(-10.5, 26.84) * mm});
            skLineSegment(sketch, "E22.right", {"start": v(-0.5, 36.34) * mm, "end": v(-0.5, 27.34) * mm});
            skLineSegment(sketch, "E23.1.0.0", {"start": v(1, 36.84) * mm, "end": v(10.5, 36.84) * mm});
            skLineSegment(sketch, "E23.1.0.1", {"start": v(0.5, 36.34) * mm, "end": v(0.5, 27.34) * mm});
            skLineSegment(sketch, "E23.1.0.2", {"start": v(1, 26.84) * mm, "end": v(10.5, 26.84) * mm});
            skLineSegment(sketch, "E23.1.0.3", {"start": v(10.5, 36.84) * mm, "end": v(10.5, 26.84) * mm});
            skLineSegment(sketch, "E23.direction1", {"start": v(-10.5, 36.84) * mm, "end": v(-1, 36.84) * mm, "construction": true});
            skPoint(sketch, "E24.visualSharp", {"position": v(-0.5, 26.84) * mm});
            skArc(sketch, "E24.filletArc", {"start": v(-1, 26.84) * mm, "mid": v(-0.65, 26.99) * mm, "end": v(-0.5, 27.34) * mm});
            skPoint(sketch, "E25.newPointA", {"position": v(0.5, 36.84) * mm});
            skPoint(sketch, "E25.newPointB", {"position": v(-0.5, 36.84) * mm});
            skArc(sketch, "E25.filletArc", {"start": v(-0.5, 36.34) * mm, "mid": v(-0.65, 36.7) * mm, "end": v(-1, 36.84) * mm});
            skArc(sketch, "E26.filletArc", {"start": v(1, 36.84) * mm, "mid": v(0.65, 36.7) * mm, "end": v(0.5, 36.34) * mm});
            skPoint(sketch, "E27.visualSharp", {"position": v(0.5, 26.84) * mm});
            skArc(sketch, "E27.filletArc", {"start": v(0.5, 27.34) * mm, "mid": v(0.65, 26.99) * mm, "end": v(1, 26.84) * mm});
            skPoint(sketch, "E28.0.1.0", {"position": v(0.5, 25.84) * mm});
            skLineSegment(sketch, "E28.0.1.1", {"start": v(-10.5, 25.84) * mm, "end": v(-1, 25.84) * mm, "construction": true});
            skLineSegment(sketch, "E28.0.1.2", {"start": v(10.5, 25.84) * mm, "end": v(10.5, 15.84) * mm});
            skLineSegment(sketch, "E28.0.1.3", {"start": v(1, 15.84) * mm, "end": v(10.5, 15.84) * mm});
            skLineSegment(sketch, "E28.0.1.4", {"start": v(0.5, 25.34) * mm, "end": v(0.5, 16.34) * mm});
            skLineSegment(sketch, "E28.0.1.5", {"start": v(1, 25.84) * mm, "end": v(10.5, 25.84) * mm});
            skLineSegment(sketch, "E28.0.1.6", {"start": v(-0.5, 25.34) * mm, "end": v(-0.5, 16.34) * mm});
            skLineSegment(sketch, "E28.0.1.7", {"start": v(-10.5, 25.84) * mm, "end": v(-10.5, 15.84) * mm});
            skLineSegment(sketch, "E28.0.1.8", {"start": v(-10.5, 15.84) * mm, "end": v(-1, 15.84) * mm});
            skPoint(sketch, "E28.0.1.9", {"position": v(-0.5, 25.84) * mm});
            skPoint(sketch, "E28.0.1.10", {"position": v(-0.5, 15.84) * mm});
            skPoint(sketch, "E28.0.1.11", {"position": v(0.5, 15.84) * mm});
            skPoint(sketch, "E28.0.1.12", {"position": v(0.5, 25.84) * mm});
            skLineSegment(sketch, "E28.0.1.13", {"start": v(-10.5, 25.84) * mm, "end": v(-0.5, 25.84) * mm});
            skArc(sketch, "E28.0.1.14", {"start": v(0.5, 16.34) * mm, "mid": v(0.65, 15.99) * mm, "end": v(1, 15.84) * mm});
            skArc(sketch, "E28.0.1.15", {"start": v(-0.5, 25.34) * mm, "mid": v(-0.65, 25.7) * mm, "end": v(-1, 25.84) * mm});
            skArc(sketch, "E28.0.1.16", {"start": v(-1, 15.84) * mm, "mid": v(-0.65, 15.99) * mm, "end": v(-0.5, 16.34) * mm});
            skArc(sketch, "E28.0.1.17", {"start": v(1, 25.84) * mm, "mid": v(0.65, 25.7) * mm, "end": v(0.5, 25.34) * mm});
            skPoint(sketch, "E28.0.2.0", {"position": v(0.5, 14.84) * mm});
            skLineSegment(sketch, "E28.0.2.1", {"start": v(-10.5, 14.84) * mm, "end": v(-1, 14.84) * mm, "construction": true});
            skLineSegment(sketch, "E28.0.2.2", {"start": v(10.5, 14.84) * mm, "end": v(10.5, 4.84) * mm});
            skLineSegment(sketch, "E28.0.2.3", {"start": v(1, 4.84) * mm, "end": v(10.5, 4.84) * mm});
            skLineSegment(sketch, "E28.0.2.4", {"start": v(0.5, 14.34) * mm, "end": v(0.5, 5.34) * mm});
            skLineSegment(sketch, "E28.0.2.5", {"start": v(1, 14.84) * mm, "end": v(10.5, 14.84) * mm});
            skLineSegment(sketch, "E28.0.2.6", {"start": v(-0.5, 14.34) * mm, "end": v(-0.5, 5.34) * mm});
            skLineSegment(sketch, "E28.0.2.7", {"start": v(-10.5, 14.84) * mm, "end": v(-10.5, 4.84) * mm});
            skLineSegment(sketch, "E28.0.2.8", {"start": v(-10.5, 4.84) * mm, "end": v(-1, 4.84) * mm});
            skPoint(sketch, "E28.0.2.9", {"position": v(-0.5, 14.84) * mm});
            skPoint(sketch, "E28.0.2.10", {"position": v(-0.5, 4.84) * mm});
            skPoint(sketch, "E28.0.2.11", {"position": v(0.5, 4.84) * mm});
            skPoint(sketch, "E28.0.2.12", {"position": v(0.5, 14.84) * mm});
            skLineSegment(sketch, "E28.0.2.13", {"start": v(-10.5, 14.84) * mm, "end": v(-0.5, 14.84) * mm});
            skArc(sketch, "E28.0.2.14", {"start": v(0.5, 5.34) * mm, "mid": v(0.65, 4.99) * mm, "end": v(1, 4.84) * mm});
            skArc(sketch, "E28.0.2.15", {"start": v(-0.5, 14.34) * mm, "mid": v(-0.65, 14.7) * mm, "end": v(-1, 14.84) * mm});
            skArc(sketch, "E28.0.2.16", {"start": v(-1, 4.84) * mm, "mid": v(-0.65, 4.99) * mm, "end": v(-0.5, 5.34) * mm});
            skArc(sketch, "E28.0.2.17", {"start": v(1, 14.84) * mm, "mid": v(0.65, 14.7) * mm, "end": v(0.5, 14.34) * mm});
            skPoint(sketch, "E28.0.3.0", {"position": v(0.5, 3.84) * mm});
            skLineSegment(sketch, "E28.0.3.1", {"start": v(-10.5, 3.84) * mm, "end": v(-1, 3.84) * mm, "construction": true});
            skLineSegment(sketch, "E28.0.3.2", {"start": v(10.5, 3.84) * mm, "end": v(10.5, -6.16) * mm});
            skLineSegment(sketch, "E28.0.3.3", {"start": v(1, -6.16) * mm, "end": v(10.5, -6.16) * mm});
            skLineSegment(sketch, "E28.0.3.4", {"start": v(0.5, 3.34) * mm, "end": v(0.5, -5.66) * mm});
            skLineSegment(sketch, "E28.0.3.5", {"start": v(1, 3.84) * mm, "end": v(10.5, 3.84) * mm});
            skLineSegment(sketch, "E28.0.3.6", {"start": v(-0.5, 3.34) * mm, "end": v(-0.5, -5.66) * mm});
            skLineSegment(sketch, "E28.0.3.7", {"start": v(-10.5, 3.84) * mm, "end": v(-10.5, -6.16) * mm});
            skLineSegment(sketch, "E28.0.3.8", {"start": v(-10.5, -6.16) * mm, "end": v(-1, -6.16) * mm});
            skPoint(sketch, "E28.0.3.9", {"position": v(-0.5, 3.84) * mm});
            skPoint(sketch, "E28.0.3.10", {"position": v(-0.5, -6.16) * mm});
            skPoint(sketch, "E28.0.3.11", {"position": v(0.5, -6.16) * mm});
            skPoint(sketch, "E28.0.3.12", {"position": v(0.5, 3.84) * mm});
            skLineSegment(sketch, "E28.0.3.13", {"start": v(-10.5, 3.84) * mm, "end": v(-0.5, 3.84) * mm});
            skArc(sketch, "E28.0.3.14", {"start": v(0.5, -5.66) * mm, "mid": v(0.65, -6.01) * mm, "end": v(1, -6.16) * mm});
            skArc(sketch, "E28.0.3.15", {"start": v(-0.5, 3.34) * mm, "mid": v(-0.65, 3.7) * mm, "end": v(-1, 3.84) * mm});
            skArc(sketch, "E28.0.3.16", {"start": v(-1, -6.16) * mm, "mid": v(-0.65, -6.01) * mm, "end": v(-0.5, -5.66) * mm});
            skArc(sketch, "E28.0.3.17", {"start": v(1, 3.84) * mm, "mid": v(0.65, 3.7) * mm, "end": v(0.5, 3.34) * mm});
            skPoint(sketch, "E28.0.4.0", {"position": v(0.5, -7.16) * mm});
            skLineSegment(sketch, "E28.0.4.1", {"start": v(-10.5, -7.16) * mm, "end": v(-1, -7.16) * mm, "construction": true});
            skLineSegment(sketch, "E28.0.4.2", {"start": v(10.5, -7.16) * mm, "end": v(10.5, -17.16) * mm});
            skLineSegment(sketch, "E28.0.4.3", {"start": v(1, -17.16) * mm, "end": v(10.5, -17.16) * mm});
            skLineSegment(sketch, "E28.0.4.4", {"start": v(0.5, -7.66) * mm, "end": v(0.5, -16.66) * mm});
            skLineSegment(sketch, "E28.0.4.5", {"start": v(1, -7.16) * mm, "end": v(10.5, -7.16) * mm});
            skLineSegment(sketch, "E28.0.4.6", {"start": v(-0.5, -7.66) * mm, "end": v(-0.5, -16.66) * mm});
            skLineSegment(sketch, "E28.0.4.7", {"start": v(-10.5, -7.16) * mm, "end": v(-10.5, -17.16) * mm});
            skLineSegment(sketch, "E28.0.4.8", {"start": v(-10.5, -17.16) * mm, "end": v(-1, -17.16) * mm});
            skPoint(sketch, "E28.0.4.9", {"position": v(-0.5, -7.16) * mm});
            skPoint(sketch, "E28.0.4.10", {"position": v(-0.5, -17.16) * mm});
            skPoint(sketch, "E28.0.4.11", {"position": v(0.5, -17.16) * mm});
            skPoint(sketch, "E28.0.4.12", {"position": v(0.5, -7.16) * mm});
            skLineSegment(sketch, "E28.0.4.13", {"start": v(-10.5, -7.16) * mm, "end": v(-0.5, -7.16) * mm});
            skArc(sketch, "E28.0.4.14", {"start": v(0.5, -16.66) * mm, "mid": v(0.65, -17.01) * mm, "end": v(1, -17.16) * mm});
            skArc(sketch, "E28.0.4.15", {"start": v(-0.5, -7.66) * mm, "mid": v(-0.65, -7.3) * mm, "end": v(-1, -7.16) * mm});
            skArc(sketch, "E28.0.4.16", {"start": v(-1, -17.16) * mm, "mid": v(-0.65, -17.01) * mm, "end": v(-0.5, -16.66) * mm});
            skArc(sketch, "E28.0.4.17", {"start": v(1, -7.16) * mm, "mid": v(0.65, -7.3) * mm, "end": v(0.5, -7.66) * mm});
            skPoint(sketch, "E28.0.5.0", {"position": v(0.5, -18.16) * mm});
            skLineSegment(sketch, "E28.0.5.1", {"start": v(-10.5, -18.16) * mm, "end": v(-1, -18.16) * mm, "construction": true});
            skLineSegment(sketch, "E28.0.5.2", {"start": v(10.5, -18.16) * mm, "end": v(10.5, -28.16) * mm});
            skLineSegment(sketch, "E28.0.5.3", {"start": v(1, -28.16) * mm, "end": v(10.5, -28.16) * mm});
            skLineSegment(sketch, "E28.0.5.4", {"start": v(0.5, -18.66) * mm, "end": v(0.5, -27.66) * mm});
            skLineSegment(sketch, "E28.0.5.5", {"start": v(1, -18.16) * mm, "end": v(10.5, -18.16) * mm});
            skLineSegment(sketch, "E28.0.5.6", {"start": v(-0.5, -18.66) * mm, "end": v(-0.5, -27.66) * mm});
            skLineSegment(sketch, "E28.0.5.7", {"start": v(-10.5, -18.16) * mm, "end": v(-10.5, -28.16) * mm});
            skLineSegment(sketch, "E28.0.5.8", {"start": v(-10.5, -28.16) * mm, "end": v(-1, -28.16) * mm});
            skPoint(sketch, "E28.0.5.9", {"position": v(-0.5, -18.16) * mm});
            skPoint(sketch, "E28.0.5.10", {"position": v(-0.5, -28.16) * mm});
            skPoint(sketch, "E28.0.5.11", {"position": v(0.5, -28.16) * mm});
            skPoint(sketch, "E28.0.5.12", {"position": v(0.5, -18.16) * mm});
            skLineSegment(sketch, "E28.0.5.13", {"start": v(-10.5, -18.16) * mm, "end": v(-0.5, -18.16) * mm});
            skArc(sketch, "E28.0.5.14", {"start": v(0.5, -27.66) * mm, "mid": v(0.65, -28.01) * mm, "end": v(1, -28.16) * mm});
            skArc(sketch, "E28.0.5.15", {"start": v(-0.5, -18.66) * mm, "mid": v(-0.65, -18.3) * mm, "end": v(-1, -18.16) * mm});
            skArc(sketch, "E28.0.5.16", {"start": v(-1, -28.16) * mm, "mid": v(-0.65, -28.01) * mm, "end": v(-0.5, -27.66) * mm});
            skArc(sketch, "E28.0.5.17", {"start": v(1, -18.16) * mm, "mid": v(0.65, -18.3) * mm, "end": v(0.5, -18.66) * mm});
            skPoint(sketch, "E28.0.6.0", {"position": v(0.5, -29.16) * mm});
            skLineSegment(sketch, "E28.0.6.1", {"start": v(-10.5, -29.16) * mm, "end": v(-1, -29.16) * mm, "construction": true});
            skLineSegment(sketch, "E28.0.6.2", {"start": v(10.5, -29.16) * mm, "end": v(10.5, -39.16) * mm});
            skLineSegment(sketch, "E28.0.6.3", {"start": v(1, -39.16) * mm, "end": v(10.5, -39.16) * mm});
            skLineSegment(sketch, "E28.0.6.4", {"start": v(0.5, -29.66) * mm, "end": v(0.5, -38.66) * mm});
            skLineSegment(sketch, "E28.0.6.5", {"start": v(1, -29.16) * mm, "end": v(10.5, -29.16) * mm});
            skLineSegment(sketch, "E28.0.6.6", {"start": v(-0.5, -29.66) * mm, "end": v(-0.5, -38.66) * mm});
            skLineSegment(sketch, "E28.0.6.7", {"start": v(-10.5, -29.16) * mm, "end": v(-10.5, -39.16) * mm});
            skLineSegment(sketch, "E28.0.6.8", {"start": v(-10.5, -39.16) * mm, "end": v(-1, -39.16) * mm});
            skPoint(sketch, "E28.0.6.9", {"position": v(-0.5, -29.16) * mm});
            skPoint(sketch, "E28.0.6.10", {"position": v(-0.5, -39.16) * mm});
            skPoint(sketch, "E28.0.6.11", {"position": v(0.5, -39.16) * mm});
            skPoint(sketch, "E28.0.6.12", {"position": v(0.5, -29.16) * mm});
            skLineSegment(sketch, "E28.0.6.13", {"start": v(-10.5, -29.16) * mm, "end": v(-0.5, -29.16) * mm});
            skArc(sketch, "E28.0.6.14", {"start": v(0.5, -38.66) * mm, "mid": v(0.65, -39.01) * mm, "end": v(1, -39.16) * mm});
            skArc(sketch, "E28.0.6.15", {"start": v(-0.5, -29.66) * mm, "mid": v(-0.65, -29.3) * mm, "end": v(-1, -29.16) * mm});
            skArc(sketch, "E28.0.6.16", {"start": v(-1, -39.16) * mm, "mid": v(-0.65, -39.01) * mm, "end": v(-0.5, -38.66) * mm});
            skArc(sketch, "E28.0.6.17", {"start": v(1, -29.16) * mm, "mid": v(0.65, -29.3) * mm, "end": v(0.5, -29.66) * mm});
            skPoint(sketch, "E28.0.7.0", {"position": v(0.5, -40.16) * mm});
            skLineSegment(sketch, "E28.0.7.1", {"start": v(-10.5, -40.16) * mm, "end": v(-1, -40.16) * mm, "construction": true});
            skLineSegment(sketch, "E28.0.7.2", {"start": v(10.5, -40.16) * mm, "end": v(10.5, -50.16) * mm});
            skLineSegment(sketch, "E28.0.7.3", {"start": v(1, -50.16) * mm, "end": v(10.5, -50.16) * mm});
            skLineSegment(sketch, "E28.0.7.4", {"start": v(0.5, -40.66) * mm, "end": v(0.5, -49.66) * mm});
            skLineSegment(sketch, "E28.0.7.5", {"start": v(1, -40.16) * mm, "end": v(10.5, -40.16) * mm});
            skLineSegment(sketch, "E28.0.7.6", {"start": v(-0.5, -40.66) * mm, "end": v(-0.5, -49.66) * mm});
            skLineSegment(sketch, "E28.0.7.7", {"start": v(-10.5, -40.16) * mm, "end": v(-10.5, -50.16) * mm});
            skLineSegment(sketch, "E28.0.7.8", {"start": v(-10.5, -50.16) * mm, "end": v(-1, -50.16) * mm});
            skPoint(sketch, "E28.0.7.9", {"position": v(-0.5, -40.16) * mm});
            skPoint(sketch, "E28.0.7.10", {"position": v(-0.5, -50.16) * mm});
            skPoint(sketch, "E28.0.7.11", {"position": v(0.5, -50.16) * mm});
            skPoint(sketch, "E28.0.7.12", {"position": v(0.5, -40.16) * mm});
            skLineSegment(sketch, "E28.0.7.13", {"start": v(-10.5, -40.16) * mm, "end": v(-0.5, -40.16) * mm});
            skArc(sketch, "E28.0.7.14", {"start": v(0.5, -49.66) * mm, "mid": v(0.65, -50.01) * mm, "end": v(1, -50.16) * mm});
            skArc(sketch, "E28.0.7.15", {"start": v(-0.5, -40.66) * mm, "mid": v(-0.65, -40.3) * mm, "end": v(-1, -40.16) * mm});
            skArc(sketch, "E28.0.7.16", {"start": v(-1, -50.16) * mm, "mid": v(-0.65, -50.01) * mm, "end": v(-0.5, -49.66) * mm});
            skArc(sketch, "E28.0.7.17", {"start": v(1, -40.16) * mm, "mid": v(0.65, -40.3) * mm, "end": v(0.5, -40.66) * mm});
            skPoint(sketch, "E28.0.8.0", {"position": v(0.5, -51.16) * mm});
            skLineSegment(sketch, "E28.0.8.1", {"start": v(-10.5, -51.16) * mm, "end": v(-1, -51.16) * mm, "construction": true});
            skLineSegment(sketch, "E28.0.8.2", {"start": v(10.5, -51.16) * mm, "end": v(10.5, -61.16) * mm});
            skLineSegment(sketch, "E28.0.8.3", {"start": v(1, -61.16) * mm, "end": v(10.5, -61.16) * mm});
            skLineSegment(sketch, "E28.0.8.4", {"start": v(0.5, -51.66) * mm, "end": v(0.5, -60.66) * mm});
            skLineSegment(sketch, "E28.0.8.5", {"start": v(1, -51.16) * mm, "end": v(10.5, -51.16) * mm});
            skLineSegment(sketch, "E28.0.8.6", {"start": v(-0.5, -51.66) * mm, "end": v(-0.5, -60.66) * mm});
            skLineSegment(sketch, "E28.0.8.7", {"start": v(-10.5, -51.16) * mm, "end": v(-10.5, -61.16) * mm});
            skLineSegment(sketch, "E28.0.8.8", {"start": v(-10.5, -61.16) * mm, "end": v(-1, -61.16) * mm});
            skPoint(sketch, "E28.0.8.9", {"position": v(-0.5, -51.16) * mm});
            skPoint(sketch, "E28.0.8.10", {"position": v(-0.5, -61.16) * mm});
            skPoint(sketch, "E28.0.8.11", {"position": v(0.5, -61.16) * mm});
            skPoint(sketch, "E28.0.8.12", {"position": v(0.5, -51.16) * mm});
            skLineSegment(sketch, "E28.0.8.13", {"start": v(-10.5, -51.16) * mm, "end": v(-0.5, -51.16) * mm});
            skArc(sketch, "E28.0.8.14", {"start": v(0.5, -60.66) * mm, "mid": v(0.65, -61.01) * mm, "end": v(1, -61.16) * mm});
            skArc(sketch, "E28.0.8.15", {"start": v(-0.5, -51.66) * mm, "mid": v(-0.65, -51.3) * mm, "end": v(-1, -51.16) * mm});
            skArc(sketch, "E28.0.8.16", {"start": v(-1, -61.16) * mm, "mid": v(-0.65, -61.01) * mm, "end": v(-0.5, -60.66) * mm});
            skArc(sketch, "E28.0.8.17", {"start": v(1, -51.16) * mm, "mid": v(0.65, -51.3) * mm, "end": v(0.5, -51.66) * mm});
            skLineSegment(sketch, "E28.direction1", {"start": v(-10.5, 26.84) * mm, "end": v(14.5, 26.84) * mm, "construction": true});
            skLineSegment(sketch, "E28.direction2", {"start": v(-10.5, 26.84) * mm, "end": v(-10.5, 15.84) * mm, "construction": true});
            skSolve(sketch);
        }
        {
            var Q0;
            {var subQ0=sQuery(id+"F6.wireOp",EDGE,"E22.left");Q0=makeQuery(id+"F6.imprint","IMPRINT",FACE,{"disambiguationData":[TD([[makeQuery(id+"F6.imprint","IMPRINT",EDGE,{"derivedFrom":subQ0}),1.0]])]});}
            var Q1;
            Q1=makeQuery(id+"F6.imprint","IMPRINT",FACE,{"disambiguationData":[TD([[makeQuery(id+"F6.imprint","IMPRINT",EDGE,{"derivedFrom":sQuery(id+"F6.wireOp",EDGE,"E23.1.0.0")}),1.0]])]});
            var Q2;
            Q2=makeQuery(id+"F6.imprint","IMPRINT",FACE,{"disambiguationData":[TD([[makeQuery(id+"F6.imprint","IMPRINT",EDGE,{"derivedFrom":sQuery(id+"F6.wireOp",EDGE,"E28.0.1.6")}),-1.0]])]});
            var Q3;
            Q3=makeQuery(id+"F6.imprint","IMPRINT",FACE,{"disambiguationData":[TD([[makeQuery(id+"F6.imprint","IMPRINT",EDGE,{"derivedFrom":sQuery(id+"F6.wireOp",EDGE,"E28.0.1.4")}),1.0]])]});
            var Q4;
            Q4=makeQuery(id+"F6.imprint","IMPRINT",FACE,{"disambiguationData":[TD([[makeQuery(id+"F6.imprint","IMPRINT",EDGE,{"derivedFrom":sQuery(id+"F6.wireOp",EDGE,"E28.0.2.6")}),-1.0]])]});
            var Q5;
            {var subQ1=sQuery(id+"F6.wireOp",EDGE,"E28.0.2.2");Q5=makeQuery(id+"F6.imprint","IMPRINT",FACE,{"disambiguationData":[TD([[makeQuery(id+"F6.imprint","IMPRINT",EDGE,{"derivedFrom":subQ1}),-1.0]])]});}
            var Q6;
            Q6=makeQuery(id+"F6.imprint","IMPRINT",FACE,{"disambiguationData":[TD([[makeQuery(id+"F6.imprint","IMPRINT",EDGE,{"derivedFrom":sQuery(id+"F6.wireOp",EDGE,"E28.0.3.6")}),-1.0]])]});
            var Q7;
            Q7=makeQuery(id+"F6.imprint","IMPRINT",FACE,{"disambiguationData":[TD([[makeQuery(id+"F6.imprint","IMPRINT",EDGE,{"derivedFrom":sQuery(id+"F6.wireOp",EDGE,"E28.0.3.4")}),1.0]])]});
            var Q8;
            Q8=makeQuery(id+"F6.imprint","IMPRINT",FACE,{"disambiguationData":[TD([[makeQuery(id+"F6.imprint","IMPRINT",EDGE,{"derivedFrom":sQuery(id+"F6.wireOp",EDGE,"E28.0.4.6")}),-1.0]])]});
            var Q9;
            {var subQ1=sQuery(id+"F6.wireOp",EDGE,"E28.0.4.2");Q9=makeQuery(id+"F6.imprint","IMPRINT",FACE,{"disambiguationData":[TD([[makeQuery(id+"F6.imprint","IMPRINT",EDGE,{"derivedFrom":subQ1}),-1.0]])]});}
            var Q10;
            Q10=makeQuery(id+"F6.imprint","IMPRINT",FACE,{"disambiguationData":[TD([[makeQuery(id+"F6.imprint","IMPRINT",EDGE,{"derivedFrom":sQuery(id+"F6.wireOp",EDGE,"E28.0.5.4")}),1.0]])]});
            var Q11;
            Q11=makeQuery(id+"F6.imprint","IMPRINT",FACE,{"disambiguationData":[TD([[makeQuery(id+"F6.imprint","IMPRINT",EDGE,{"derivedFrom":sQuery(id+"F6.wireOp",EDGE,"E28.0.6.6")}),-1.0]])]});
            var Q12;
            Q12=makeQuery(id+"F6.imprint","IMPRINT",FACE,{"disambiguationData":[TD([[makeQuery(id+"F6.imprint","IMPRINT",EDGE,{"derivedFrom":sQuery(id+"F6.wireOp",EDGE,"E28.0.5.6")}),-1.0]])]});
            var Q13;
            {var subQ1=sQuery(id+"F6.wireOp",EDGE,"E28.0.6.2");Q13=makeQuery(id+"F6.imprint","IMPRINT",FACE,{"disambiguationData":[TD([[makeQuery(id+"F6.imprint","IMPRINT",EDGE,{"derivedFrom":subQ1}),-1.0]])]});}
            var Q14;
            Q14=makeQuery(id+"F6.imprint","IMPRINT",FACE,{"disambiguationData":[TD([[makeQuery(id+"F6.imprint","IMPRINT",EDGE,{"derivedFrom":sQuery(id+"F6.wireOp",EDGE,"E28.0.7.6")}),-1.0]])]});
            var Q15;
            Q15=makeQuery(id+"F6.imprint","IMPRINT",FACE,{"disambiguationData":[TD([[makeQuery(id+"F6.imprint","IMPRINT",EDGE,{"derivedFrom":sQuery(id+"F6.wireOp",EDGE,"E28.0.7.4")}),1.0]])]});
            var Q16;
            Q16=makeQuery(id+"F6.imprint","IMPRINT",FACE,{"disambiguationData":[TD([[makeQuery(id+"F6.imprint","IMPRINT",EDGE,{"derivedFrom":sQuery(id+"F6.wireOp",EDGE,"E28.0.8.6")}),-1.0]])]});
            var Q17;
            {var subQ1=sQuery(id+"F6.wireOp",EDGE,"E28.0.8.2");Q17=makeQuery(id+"F6.imprint","IMPRINT",FACE,{"disambiguationData":[TD([[makeQuery(id+"F6.imprint","IMPRINT",EDGE,{"derivedFrom":subQ1}),-1.0]])]});}
            extrude(context, id + "F7", {"entities" : qUnion([Q0, Q1, Q2, Q3, Q4, Q5, Q6, Q7, Q8, Q9, Q10, Q11, Q12, Q13, Q14, Q15, Q16, Q17]), "operationType" : NewBodyOperationType.ADD, "depth" : 0.5 * mm, "offsetDistance" : 25 * mm});
        }
        {
            var Q0;
            Q0=makeQuery(id+"F7.boolean.opBoolean","MERGE",FACE,{"derivedFrom":[makeQuery(id+"F5.boolean.opBoolean","MERGE",FACE,{"derivedFrom":[makeQuery(id+"F3.boolean.opBoolean","MERGE",FACE,{"derivedFrom":[makeQuery(id+"F1.opExtrude","SWEPT_FACE",FACE,{"disambiguationData":[OSD([sQuery(id+"F0.wireOp",EDGE,"E0.bottom")])]}),makeQuery(id+"F3.opExtrude","SWEPT_FACE",FACE,{"disambiguationData":[OSD([sQuery(id+"F2.wireOp",EDGE,"E1.bottom")])]}),makeQuery(id+"F3.opExtrude","SWEPT_FACE",FACE,{"disambiguationData":[OSD([sQuery(id+"F2.wireOp",EDGE,"E6.1.0.3")])]}),makeQuery(id+"F3.opExtrude","SWEPT_FACE",FACE,{"disambiguationData":[OSD([sQuery(id+"F2.wireOp",EDGE,"E6.2.0.3")])]}),makeQuery(id+"F3.opExtrude","SWEPT_FACE",FACE,{"disambiguationData":[OSD([sQuery(id+"F2.wireOp",EDGE,"E6.3.0.3")])]})]}),makeQuery(id+"F5.opExtrude","SWEPT_FACE",FACE,{"disambiguationData":[OSD([sQuery(id+"F4.wireOp",EDGE,"E15.bottom")])]}),makeQuery(id+"F5.opExtrude","SWEPT_FACE",FACE,{"disambiguationData":[OSD([sQuery(id+"F4.wireOp",EDGE,"E16.1.0.0")])]})]}),makeQuery(id+"F7.opExtrude","SWEPT_FACE",FACE,{"disambiguationData":[OSD([sQuery(id+"F6.wireOp",EDGE,"E22.bottom")])]}),makeQuery(id+"F7.opExtrude","SWEPT_FACE",FACE,{"disambiguationData":[OSD([sQuery(id+"F6.wireOp",EDGE,"E23.1.0.0")])]})]});
            var sketch = newSketch(context, id + "F8", { "sketchPlane" : qUnion([Q0])});
            skLineSegment(sketch, "E29.bottom", {"start": v(37.91, 10.5) * mm, "end": v(17.91, 10.5) * mm});
            skLineSegment(sketch, "E29.top", {"start": v(37.91, 0.5) * mm, "end": v(17.91, 0.5) * mm});
            skLineSegment(sketch, "E29.left", {"start": v(37.91, 10.5) * mm, "end": v(37.91, 0.5) * mm});
            skLineSegment(sketch, "E29.right", {"start": v(17.91, 10.5) * mm, "end": v(17.91, 0.5) * mm});
            skLineSegment(sketch, "E30.0.1.0", {"start": v(17.91, -0.5) * mm, "end": v(17.91, -10.5) * mm});
            skLineSegment(sketch, "E30.0.1.1", {"start": v(37.91, -0.5) * mm, "end": v(17.91, -0.5) * mm});
            skLineSegment(sketch, "E30.0.1.2", {"start": v(37.91, -0.5) * mm, "end": v(37.91, -10.5) * mm});
            skLineSegment(sketch, "E30.0.1.3", {"start": v(37.91, -10.5) * mm, "end": v(17.91, -10.5) * mm});
            skLineSegment(sketch, "E30.1.0.0", {"start": v(-3.09, 10.5) * mm, "end": v(-3.09, 0.5) * mm});
            skLineSegment(sketch, "E30.1.0.1", {"start": v(16.91, 10.5) * mm, "end": v(-3.09, 10.5) * mm});
            skLineSegment(sketch, "E30.1.0.2", {"start": v(16.91, 10.5) * mm, "end": v(16.91, 0.5) * mm});
            skLineSegment(sketch, "E30.1.0.3", {"start": v(16.91, 0.5) * mm, "end": v(-3.09, 0.5) * mm});
            skLineSegment(sketch, "E30.1.1.0", {"start": v(-3.09, -0.5) * mm, "end": v(-3.09, -10.5) * mm});
            skLineSegment(sketch, "E30.1.1.1", {"start": v(16.91, -0.5) * mm, "end": v(-3.09, -0.5) * mm});
            skLineSegment(sketch, "E30.1.1.2", {"start": v(16.91, -0.5) * mm, "end": v(16.91, -10.5) * mm});
            skLineSegment(sketch, "E30.1.1.3", {"start": v(16.91, -10.5) * mm, "end": v(-3.09, -10.5) * mm});
            skLineSegment(sketch, "E30.2.0.0", {"start": v(-24.09, 10.5) * mm, "end": v(-24.09, 0.5) * mm});
            skLineSegment(sketch, "E30.2.0.1", {"start": v(-4.09, 10.5) * mm, "end": v(-24.09, 10.5) * mm});
            skLineSegment(sketch, "E30.2.0.2", {"start": v(-4.09, 10.5) * mm, "end": v(-4.09, 0.5) * mm});
            skLineSegment(sketch, "E30.2.0.3", {"start": v(-4.09, 0.5) * mm, "end": v(-24.09, 0.5) * mm});
            skLineSegment(sketch, "E30.2.1.0", {"start": v(-24.09, -0.5) * mm, "end": v(-24.09, -10.5) * mm});
            skLineSegment(sketch, "E30.2.1.1", {"start": v(-4.09, -0.5) * mm, "end": v(-24.09, -0.5) * mm});
            skLineSegment(sketch, "E30.2.1.2", {"start": v(-4.09, -0.5) * mm, "end": v(-4.09, -10.5) * mm});
            skLineSegment(sketch, "E30.2.1.3", {"start": v(-4.09, -10.5) * mm, "end": v(-24.09, -10.5) * mm});
            skLineSegment(sketch, "E30.3.0.0", {"start": v(-45.09, 10.5) * mm, "end": v(-45.09, 0.5) * mm});
            skLineSegment(sketch, "E30.3.0.1", {"start": v(-25.09, 10.5) * mm, "end": v(-45.09, 10.5) * mm});
            skLineSegment(sketch, "E30.3.0.2", {"start": v(-25.09, 10.5) * mm, "end": v(-25.09, 0.5) * mm});
            skLineSegment(sketch, "E30.3.0.3", {"start": v(-25.09, 0.5) * mm, "end": v(-45.09, 0.5) * mm});
            skLineSegment(sketch, "E30.3.1.0", {"start": v(-45.09, -0.5) * mm, "end": v(-45.09, -10.5) * mm});
            skLineSegment(sketch, "E30.3.1.1", {"start": v(-25.09, -0.5) * mm, "end": v(-45.09, -0.5) * mm});
            skLineSegment(sketch, "E30.3.1.2", {"start": v(-25.09, -0.5) * mm, "end": v(-25.09, -10.5) * mm});
            skLineSegment(sketch, "E30.3.1.3", {"start": v(-25.09, -10.5) * mm, "end": v(-45.09, -10.5) * mm});
            skLineSegment(sketch, "E30.direction1", {"start": v(17.91, 0.5) * mm, "end": v(-3.09, 0.5) * mm, "construction": true});
            skLineSegment(sketch, "E30.direction2", {"start": v(17.91, 0.5) * mm, "end": v(17.91, -10.5) * mm, "construction": true});
            skSolve(sketch);
        }
        {
            var Q0;
            {var subQ5=sQuery(id+"F0.wireOp",EDGE,"E0.right");var subQ6=sQuery(id+"F0.wireOp",EDGE,"E0.bottom");var subQ16=sQuery(id+"F4.wireOp",EDGE,"E16.1.0.0");var subQ25=makeQuery(id+"F5.opExtrude","SWEPT_EDGE",EDGE,{"disambiguationData":[OSD([subQ6,subQ5,subQ16,sQuery(id+"F4.wireOp",EDGE,"E19.filletArc")])]});Q0=makeQuery(id+"F8.imprint","IMPRINT",FACE,{"disambiguationData":[TD([[makeQuery(id+"F8.imprint","IMPRINT",EDGE,{"derivedFrom":subQ25}),-1.0]])]});}
            var Q1;
            {var subQ14=sQuery(id+"F2.wireOp",EDGE,"E1.bottom");var subQ23=makeQuery(id+"F3.opExtrude","CAP_EDGE",EDGE,{"disambiguationData":[OSD([subQ14])],"isStart":false});Q1=makeQuery(id+"F8.imprint","IMPRINT",FACE,{"disambiguationData":[TD([[makeQuery(id+"F8.imprint","IMPRINT",EDGE,{"derivedFrom":subQ23}),1.0]])]});}
            var Q2;
            {var subQ22=sQuery(id+"F8.wireOp",EDGE,"E30.1.0.3");Q2=makeQuery(id+"F8.imprint","IMPRINT",FACE,{"disambiguationData":[TD([[makeQuery(id+"F8.imprint","IMPRINT",EDGE,{"derivedFrom":subQ22}),-1.0]])]});}
            var Q3;
            {var subQ1=sQuery(id+"F8.wireOp",EDGE,"E30.1.1.1");Q3=makeQuery(id+"F8.imprint","IMPRINT",FACE,{"disambiguationData":[TD([[makeQuery(id+"F8.imprint","IMPRINT",EDGE,{"derivedFrom":subQ1}),1.0]])]});}
            var Q4;
            {var subQ1=sQuery(id+"F8.wireOp",EDGE,"E30.2.1.1");Q4=makeQuery(id+"F8.imprint","IMPRINT",FACE,{"disambiguationData":[TD([[makeQuery(id+"F8.imprint","IMPRINT",EDGE,{"derivedFrom":subQ1}),1.0]])]});}
            var Q5;
            {var subQ20=sQuery(id+"F6.wireOp",EDGE,"E22.bottom");var subQ22=makeQuery(id+"F7.opExtrude","SWEPT_EDGE",EDGE,{"disambiguationData":[OSD([subQ20,sQuery(id+"F6.wireOp",EDGE,"E25.filletArc")])]});Q5=makeQuery(id+"F8.imprint","IMPRINT",FACE,{"disambiguationData":[TD([[makeQuery(id+"F8.imprint","IMPRINT",EDGE,{"derivedFrom":subQ22}),1.0]])]});}
            var Q6;
            {var subQ0=sQuery(id+"F6.wireOp",EDGE,"E23.1.0.0");Q6=makeQuery(id+"F8.imprint","IMPRINT",FACE,{"disambiguationData":[TD([[makeQuery(id+"F8.imprint","IMPRINT",EDGE,{"derivedFrom":makeQuery(id+"F7.opExtrude","CAP_EDGE",EDGE,{"disambiguationData":[OSD([subQ0])],"isStart":false})}),-1.0]])]});}
            var Q7;
            {var subQ20=sQuery(id+"F8.wireOp",EDGE,"E30.2.0.3");Q7=makeQuery(id+"F8.imprint","IMPRINT",FACE,{"disambiguationData":[TD([[makeQuery(id+"F8.imprint","IMPRINT",EDGE,{"derivedFrom":subQ20}),-1.0]])]});}
            extrude(context, id + "F9", {"entities" : qUnion([Q0, Q1, Q2, Q3, Q4, Q5, Q6, Q7]), "operationType" : NewBodyOperationType.ADD, "depth" : 0.5 * mm, "offsetDistance" : 25 * mm});
        }
        {
            var Q0;
            Q0=makeQuery(id+"F3.opExtrude","CAP_FACE",FACE,{"disambiguationData":[OSD([sQuery(id+"F2.wireOp",EDGE,"E13.0.3.7"),sQuery(id+"F2.wireOp",EDGE,"E13.0.3.9"),sQuery(id+"F2.wireOp",EDGE,"E13.0.3.12"),sQuery(id+"F2.wireOp",EDGE,"E13.0.3.20"),sQuery(id+"F2.wireOp",EDGE,"E13.0.3.49"),sQuery(id+"F2.wireOp",EDGE,"E13.0.3.51"),sQuery(id+"F2.wireOp",EDGE,"E13.0.3.52"),sQuery(id+"F2.wireOp",EDGE,"E13.0.3.71")])],"isStart":true});
            var Q1;
            Q1=makeQuery(id+"F7.boolean.opBoolean","MERGE",FACE,{"derivedFrom":[makeQuery(id+"F3.opExtrude","CAP_FACE",FACE,{"disambiguationData":[OSD([sQuery(id+"F2.wireOp",EDGE,"E13.0.3.21"),sQuery(id+"F2.wireOp",EDGE,"E13.0.3.24"),sQuery(id+"F2.wireOp",EDGE,"E13.0.3.29"),sQuery(id+"F2.wireOp",EDGE,"E13.0.3.41"),sQuery(id+"F2.wireOp",EDGE,"E13.0.3.55"),sQuery(id+"F2.wireOp",EDGE,"E13.0.3.69"),sQuery(id+"F2.wireOp",EDGE,"E13.0.3.70"),sQuery(id+"F2.wireOp",EDGE,"E13.0.3.72")])],"isStart":true}),makeQuery(id+"F7.opExtrude","SWEPT_FACE",FACE,{"disambiguationData":[OSD([sQuery(id+"F6.wireOp",EDGE,"E28.0.7.7")])]})]});
            var Q2;
            Q2=makeQuery(id+"F3.opExtrude","CAP_FACE",FACE,{"disambiguationData":[OSD([sQuery(id+"F2.wireOp",EDGE,"E13.0.2.1"),sQuery(id+"F2.wireOp",EDGE,"E13.0.2.32"),sQuery(id+"F2.wireOp",EDGE,"E13.0.2.35"),sQuery(id+"F2.wireOp",EDGE,"E13.0.2.37"),sQuery(id+"F2.wireOp",EDGE,"E13.0.2.42"),sQuery(id+"F2.wireOp",EDGE,"E13.0.2.45"),sQuery(id+"F2.wireOp",EDGE,"E13.0.2.65"),sQuery(id+"F2.wireOp",EDGE,"E13.0.2.67")])],"isStart":true});
            var Q3;
            Q3=makeQuery(id+"F3.opExtrude","CAP_FACE",FACE,{"disambiguationData":[OSD([sQuery(id+"F2.wireOp",EDGE,"E13.0.1.3"),sQuery(id+"F2.wireOp",EDGE,"E13.0.1.11"),sQuery(id+"F2.wireOp",EDGE,"E13.0.1.14"),sQuery(id+"F2.wireOp",EDGE,"E13.0.1.25"),sQuery(id+"F2.wireOp",EDGE,"E13.0.1.50"),sQuery(id+"F2.wireOp",EDGE,"E13.0.1.53"),sQuery(id+"F2.wireOp",EDGE,"E13.0.1.60"),sQuery(id+"F2.wireOp",EDGE,"E13.0.1.61")])],"isStart":true});
            var Q4;
            Q4=makeQuery(id+"F3.opExtrude","CAP_FACE",FACE,{"disambiguationData":[OSD([sQuery(id+"F2.wireOp",EDGE,"E13.0.1.23"),sQuery(id+"F2.wireOp",EDGE,"E13.0.1.26"),sQuery(id+"F2.wireOp",EDGE,"E13.0.1.28"),sQuery(id+"F2.wireOp",EDGE,"E13.0.1.30"),sQuery(id+"F2.wireOp",EDGE,"E13.0.1.46"),sQuery(id+"F2.wireOp",EDGE,"E13.0.1.48"),sQuery(id+"F2.wireOp",EDGE,"E13.0.1.54"),sQuery(id+"F2.wireOp",EDGE,"E13.0.1.56")])],"isStart":true});
            var Q5;
            Q5=makeQuery(id+"F3.opExtrude","CAP_FACE",FACE,{"disambiguationData":[OSD([sQuery(id+"F2.wireOp",EDGE,"E12.2.0.0"),sQuery(id+"F2.wireOp",EDGE,"E12.2.0.1"),sQuery(id+"F2.wireOp",EDGE,"E12.2.0.2"),sQuery(id+"F2.wireOp",EDGE,"E12.2.0.3"),sQuery(id+"F2.wireOp",EDGE,"E12.2.0.4"),sQuery(id+"F2.wireOp",EDGE,"E12.2.0.5"),sQuery(id+"F2.wireOp",EDGE,"E12.2.0.6"),sQuery(id+"F2.wireOp",EDGE,"E12.2.0.7")])],"isStart":true});
            extrude(context, id + "F10", {"entities" : qUnion([Q0, Q1, Q2, Q3, Q4, Q5]), "operationType" : NewBodyOperationType.REMOVE, "oppositeDirection" : true, "depth" : 10 * mm, "offsetDistance" : 25 * mm});
        }
        {
            var Q0;
            Q0=makeQuery(id+"F5.opExtrude","CAP_FACE",FACE,{"disambiguationData":[OSD([sQuery(id+"F0.wireOp",EDGE,"E0.right"),sQuery(id+"F2.wireOp",EDGE,"E13.0.3.9"),sQuery(id+"F2.wireOp",EDGE,"E13.0.3.49"),sQuery(id+"F2.wireOp",EDGE,"E13.0.3.51"),sQuery(id+"F4.wireOp",EDGE,"E21.0.6.2"),sQuery(id+"F4.wireOp",EDGE,"E21.0.6.3"),sQuery(id+"F4.wireOp",EDGE,"E21.0.6.4"),sQuery(id+"F4.wireOp",EDGE,"E21.0.6.5"),sQuery(id+"F4.wireOp",EDGE,"E21.0.6.14"),sQuery(id+"F4.wireOp",EDGE,"E21.0.6.17")])],"isStart":false});
            var Q1;
            Q1=makeQuery(id+"F10.boolean.opBoolean","COPY",FACE,{"derivedFrom":makeQuery(id+"F10.opExtrude","SWEPT_FACE",FACE,{"disambiguationData":[OSD([sQuery(id+"F2.wireOp",EDGE,"E13.0.3.9")])]})});
            extrude(context, id + "F11", {"entities" : qUnion([Q0]), "operationType" : NewBodyOperationType.REMOVE, "endBound" : BoundingType.UP_TO_SURFACE, "oppositeDirection" : true, "depth" : 25 * mm, "endBoundEntityFace" : qUnion([Q1]), "offsetDistance" : 25 * mm});
        }
        {
            var Q0;
            Q0=makeQuery(id+"F3.opExtrude","CAP_FACE",FACE,{"disambiguationData":[OSD([sQuery(id+"F2.wireOp",EDGE,"E13.0.2.1"),sQuery(id+"F2.wireOp",EDGE,"E13.0.2.32"),sQuery(id+"F2.wireOp",EDGE,"E13.0.2.35"),sQuery(id+"F2.wireOp",EDGE,"E13.0.2.37"),sQuery(id+"F2.wireOp",EDGE,"E13.0.2.42"),sQuery(id+"F2.wireOp",EDGE,"E13.0.2.45"),sQuery(id+"F2.wireOp",EDGE,"E13.0.2.65"),sQuery(id+"F2.wireOp",EDGE,"E13.0.2.67")])],"isStart":false});
            var Q1;
            Q1=makeQuery(id+"F3.opExtrude","CAP_FACE",FACE,{"disambiguationData":[OSD([sQuery(id+"F2.wireOp",EDGE,"E13.0.1.1"),sQuery(id+"F2.wireOp",EDGE,"E13.0.1.32"),sQuery(id+"F2.wireOp",EDGE,"E13.0.1.35"),sQuery(id+"F2.wireOp",EDGE,"E13.0.1.37"),sQuery(id+"F2.wireOp",EDGE,"E13.0.1.42"),sQuery(id+"F2.wireOp",EDGE,"E13.0.1.45"),sQuery(id+"F2.wireOp",EDGE,"E13.0.1.65"),sQuery(id+"F2.wireOp",EDGE,"E13.0.1.67")])],"isStart":false});
            var Q2;
            Q2=makeQuery(id+"F3.opExtrude","CAP_FACE",FACE,{"disambiguationData":[OSD([sQuery(id+"F2.wireOp",EDGE,"E12.2.0.0"),sQuery(id+"F2.wireOp",EDGE,"E12.2.0.1"),sQuery(id+"F2.wireOp",EDGE,"E12.2.0.2"),sQuery(id+"F2.wireOp",EDGE,"E12.2.0.3"),sQuery(id+"F2.wireOp",EDGE,"E12.2.0.4"),sQuery(id+"F2.wireOp",EDGE,"E12.2.0.5"),sQuery(id+"F2.wireOp",EDGE,"E12.2.0.6"),sQuery(id+"F2.wireOp",EDGE,"E12.2.0.7")])],"isStart":false});
            extrude(context, id + "F12", {"entities" : qUnion([Q0, Q1, Q2]), "operationType" : NewBodyOperationType.REMOVE, "oppositeDirection" : true, "depth" : 10 * mm, "offsetDistance" : 25 * mm});
        }
        {
            var Q0;
            {var subQ0=sQuery(id+"F2.wireOp",EDGE,"E13.0.3.33");var subQ1=sQuery(id+"F0.wireOp",EDGE,"E0.right");var subQ2=makeQuery(id+"F1.opExtrude","CAP_EDGE",EDGE,{"disambiguationData":[OSD([subQ1])],"isStart":false});var subQ3=sQuery(id+"F2.wireOp",EDGE,"E13.0.3.38");Q0=makeQuery(id+"F5.boolean.opBoolean","MERGE",FACE,{"derivedFrom":[makeQuery(id+"F3.opExtrude","CAP_FACE",FACE,{"disambiguationData":[OSD([subQ1,sQuery(id+"F2.wireOp",EDGE,"E13.0.3.16"),subQ0,subQ3,sQuery(id+"F2.wireOp",EDGE,"E13.0.3.47"),sQuery(id+"F2.wireOp",EDGE,"E13.0.3.68")])],"isStart":false}),makeQuery(id+"F5.opExtrude","SWEPT_FACE",FACE,{"disambiguationData":[OSD([subQ1]),TDD([makeQuery(id+"F4.imprint","IMPRINT",EDGE,{"derivedFrom":makeQuery(id+"F3.opExtrude","CAP_EDGE",EDGE,{"disambiguationData":[OSD([subQ1]),TDD([makeQuery(id+"F2.imprint","IMPRINT",EDGE,{"disambiguationData":[TD([[makeQuery(id+"F2.imprint","INTERSECT",VERTEX,{"derivedFrom":[subQ2,subQ0]}),1.0]])],"derivedFrom":subQ2})])],"isStart":false})})])]})]});}
            var Q1;
            {var subQ0=sQuery(id+"F2.wireOp",EDGE,"E13.0.2.9");Q1=makeQuery(id+"F5.boolean.opBoolean","MERGE",FACE,{"derivedFrom":[makeQuery(id+"F3.opExtrude","CAP_FACE",FACE,{"disambiguationData":[OSD([sQuery(id+"F2.wireOp",EDGE,"E13.0.2.7"),subQ0,sQuery(id+"F2.wireOp",EDGE,"E13.0.2.12"),sQuery(id+"F2.wireOp",EDGE,"E13.0.2.20"),sQuery(id+"F2.wireOp",EDGE,"E13.0.2.49"),sQuery(id+"F2.wireOp",EDGE,"E13.0.2.51"),sQuery(id+"F2.wireOp",EDGE,"E13.0.2.52"),sQuery(id+"F2.wireOp",EDGE,"E13.0.2.71")])],"isStart":false}),makeQuery(id+"F5.opExtrude","SWEPT_FACE",FACE,{"disambiguationData":[OSD([subQ0])]})]});}
            var Q2;
            Q2=makeQuery(id+"F7.boolean.opBoolean","MERGE",FACE,{"derivedFrom":[makeQuery(id+"F3.opExtrude","CAP_FACE",FACE,{"disambiguationData":[OSD([sQuery(id+"F0.wireOp",EDGE,"E0.left"),sQuery(id+"F2.wireOp",EDGE,"E13.0.2.0"),sQuery(id+"F2.wireOp",EDGE,"E13.0.2.17"),sQuery(id+"F2.wireOp",EDGE,"E13.0.2.40"),sQuery(id+"F2.wireOp",EDGE,"E13.0.2.62"),sQuery(id+"F2.wireOp",EDGE,"E13.0.2.63")])],"isStart":false}),makeQuery(id+"F7.opExtrude","SWEPT_FACE",FACE,{"disambiguationData":[OSD([sQuery(id+"F6.wireOp",EDGE,"E28.0.4.2")])]})]});
            extrude(context, id + "F13", {"entities" : qUnion([Q0, Q1, Q2]), "operationType" : NewBodyOperationType.REMOVE, "oppositeDirection" : true, "depth" : 10 * mm, "offsetDistance" : 25 * mm});
        }
        {
            var Q0;
            {var subQ0=sQuery(id+"F6.wireOp",EDGE,"E23.1.0.3");var subQ1=sQuery(id+"F2.wireOp",EDGE,"E6.3.0.3");Q0=makeQuery(id+"F9.boolean.opBoolean","MERGE",FACE,{"derivedFrom":[makeQuery(id+"F7.boolean.opBoolean","MERGE",FACE,{"derivedFrom":[makeQuery(id+"F3.opExtrude","CAP_FACE",FACE,{"disambiguationData":[OSD([sQuery(id+"F0.wireOp",EDGE,"E0.left"),sQuery(id+"F2.wireOp",EDGE,"E6.3.0.1"),sQuery(id+"F2.wireOp",EDGE,"E6.3.0.2"),subQ1,sQuery(id+"F2.wireOp",EDGE,"E6.3.0.6"),sQuery(id+"F2.wireOp",EDGE,"E6.3.0.7")])],"isStart":false}),makeQuery(id+"F7.opExtrude","SWEPT_FACE",FACE,{"disambiguationData":[OSD([subQ0])]})]}),makeQuery(id+"F9.opExtrude","SWEPT_FACE",FACE,{"disambiguationData":[OSD([subQ1,sQuery(id+"F6.wireOp",EDGE,"E23.1.0.0"),subQ0])]})]});}
            extrude(context, id + "F14", {"entities" : qUnion([Q0]), "operationType" : NewBodyOperationType.REMOVE, "oppositeDirection" : true, "depth" : 10 * mm, "offsetDistance" : 25 * mm});
        }
    });
